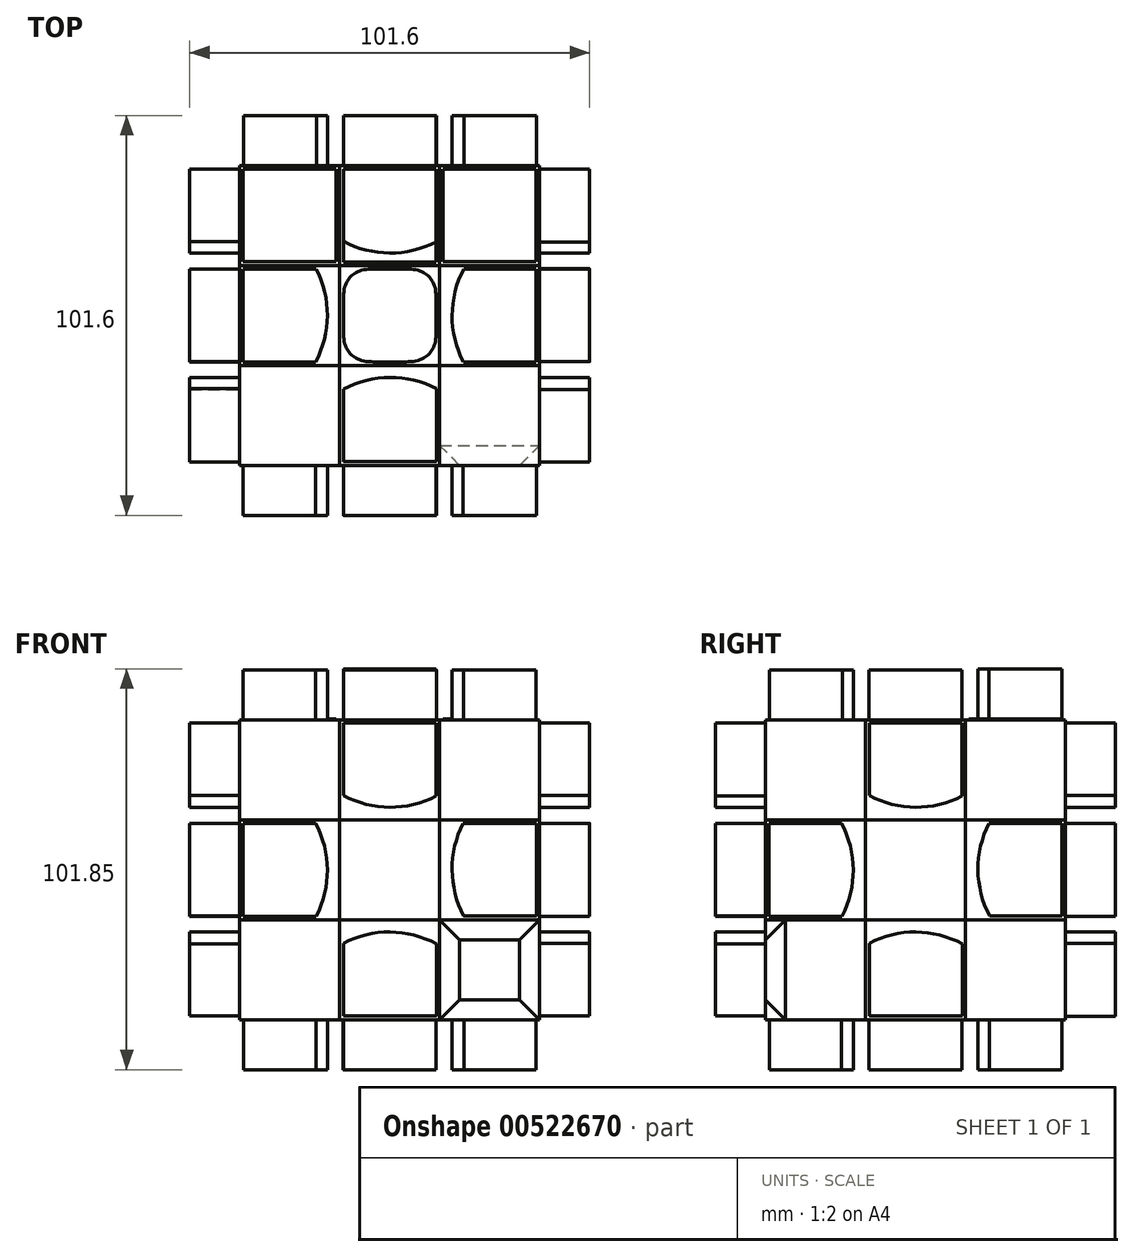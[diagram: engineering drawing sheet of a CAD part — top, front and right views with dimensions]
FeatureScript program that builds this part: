
annotation { "Feature Type Name" : "Feature", "Feature Type Description" : "" }
export const myFeature = defineFeature(function(context is Context, id is Id, definition is map)
    precondition{}
    {
        {
            var Q0;
            Q0=qCreatedBy(makeId("Top.planeOp"),FACE);
            var sketch = newSketch(context, id + "F0", { "sketchPlane" : qUnion([Q0])});
            skLineSegment(sketch, "E0.bottom", {"start": v(12.7, 12.7) * mm, "end": v(-12.7, 12.7) * mm});
            skLineSegment(sketch, "E0.top", {"start": v(12.7, -12.7) * mm, "end": v(-12.7, -12.7) * mm});
            skLineSegment(sketch, "E0.left", {"start": v(12.7, 12.7) * mm, "end": v(12.7, -12.7) * mm});
            skLineSegment(sketch, "E0.right", {"start": v(-12.7, 12.7) * mm, "end": v(-12.7, -12.7) * mm});
            skPoint(sketch, "E0.middle", {"position": v(0, 0) * mm});
            skSolve(sketch);
        }
        {
            var Q0;
            Q0=makeQuery(id+"F0.imprint","IMPRINT",FACE,{"disambiguationData":[TD([[makeQuery(id+"F0.imprint","IMPRINT",EDGE,{"derivedFrom":sQuery(id+"F0.wireOp",EDGE,"E0.bottom")}),1.0]])]});
            var sketch = newSketch(context, id + "F1", { "sketchPlane" : qUnion([Q0])});
            skLineSegment(sketch, "E1.bottom", {"start": v(-12.7, 12.7) * mm, "end": v(-38.1, 12.7) * mm});
            skLineSegment(sketch, "E1.top", {"start": v(-12.7, 38.1) * mm, "end": v(-38.1, 38.1) * mm});
            skLineSegment(sketch, "E1.left", {"start": v(-12.7, 12.7) * mm, "end": v(-12.7, 38.1) * mm});
            skLineSegment(sketch, "E1.right", {"start": v(-38.1, 12.7) * mm, "end": v(-38.1, 38.1) * mm});
            skSolve(sketch);
        }
        {
            var Q0;
            Q0=qCreatedBy(makeId("Top.planeOp"),FACE);
            var sketch = newSketch(context, id + "F2", { "sketchPlane" : qUnion([Q0])});
            skLineSegment(sketch, "E2.bottom", {"start": v(-12.7, 12.7) * mm, "end": v(12.7, 12.7) * mm});
            skLineSegment(sketch, "E2.top", {"start": v(-12.7, 38.1) * mm, "end": v(12.7, 38.1) * mm});
            skLineSegment(sketch, "E2.left", {"start": v(-12.7, 12.7) * mm, "end": v(-12.7, 38.1) * mm});
            skLineSegment(sketch, "E2.right", {"start": v(12.7, 12.7) * mm, "end": v(12.7, 38.1) * mm});
            skSolve(sketch);
        }
        {
            var Q0;
            Q0=qCreatedBy(makeId("Top.planeOp"),FACE);
            var sketch = newSketch(context, id + "F3", { "sketchPlane" : qUnion([Q0])});
            skLineSegment(sketch, "E3.bottom", {"start": v(12.7, 38.1) * mm, "end": v(38.1, 38.1) * mm});
            skLineSegment(sketch, "E3.top", {"start": v(12.7, 12.7) * mm, "end": v(38.1, 12.7) * mm});
            skLineSegment(sketch, "E3.left", {"start": v(12.7, 38.1) * mm, "end": v(12.7, 12.7) * mm});
            skLineSegment(sketch, "E3.right", {"start": v(38.1, 38.1) * mm, "end": v(38.1, 12.7) * mm});
            skSolve(sketch);
        }
        {
            var Q0;
            Q0=qCreatedBy(makeId("Top.planeOp"),FACE);
            var sketch = newSketch(context, id + "F4", { "sketchPlane" : qUnion([Q0])});
            skLineSegment(sketch, "E4.bottom", {"start": v(12.7, 12.7) * mm, "end": v(38.1, 12.7) * mm});
            skLineSegment(sketch, "E4.top", {"start": v(12.7, -12.7) * mm, "end": v(38.1, -12.7) * mm});
            skLineSegment(sketch, "E4.left", {"start": v(12.7, 12.7) * mm, "end": v(12.7, -12.7) * mm});
            skLineSegment(sketch, "E4.right", {"start": v(38.1, 12.7) * mm, "end": v(38.1, -12.7) * mm});
            skSolve(sketch);
        }
        {
            var Q0;
            Q0=qCreatedBy(makeId("Top.planeOp"),FACE);
            var sketch = newSketch(context, id + "F5", { "sketchPlane" : qUnion([Q0])});
            skLineSegment(sketch, "E5.bottom", {"start": v(12.7, -12.7) * mm, "end": v(38.1, -12.7) * mm});
            skLineSegment(sketch, "E5.top", {"start": v(12.7, -38.1) * mm, "end": v(38.1, -38.1) * mm});
            skLineSegment(sketch, "E5.left", {"start": v(12.7, -12.7) * mm, "end": v(12.7, -38.1) * mm});
            skLineSegment(sketch, "E5.right", {"start": v(38.1, -12.7) * mm, "end": v(38.1, -38.1) * mm});
            skSolve(sketch);
        }
        {
            var Q0;
            Q0=qCreatedBy(makeId("Top.planeOp"),FACE);
            var sketch = newSketch(context, id + "F6", { "sketchPlane" : qUnion([Q0])});
            skLineSegment(sketch, "E6.bottom", {"start": v(12.7, -12.7) * mm, "end": v(-12.7, -12.7) * mm});
            skLineSegment(sketch, "E6.top", {"start": v(12.7, -38.1) * mm, "end": v(-12.7, -38.1) * mm});
            skLineSegment(sketch, "E6.left", {"start": v(12.7, -12.7) * mm, "end": v(12.7, -38.1) * mm});
            skLineSegment(sketch, "E6.right", {"start": v(-12.7, -12.7) * mm, "end": v(-12.7, -38.1) * mm});
            skSolve(sketch);
        }
        {
            var Q0;
            Q0=qCreatedBy(makeId("Top.planeOp"),FACE);
            var sketch = newSketch(context, id + "F7", { "sketchPlane" : qUnion([Q0])});
            skLineSegment(sketch, "E7.bottom", {"start": v(-12.7, 12.7) * mm, "end": v(-38.1, 12.7) * mm});
            skLineSegment(sketch, "E7.top", {"start": v(-12.7, -12.7) * mm, "end": v(-38.1, -12.7) * mm});
            skLineSegment(sketch, "E7.left", {"start": v(-12.7, 12.7) * mm, "end": v(-12.7, -12.7) * mm});
            skLineSegment(sketch, "E7.right", {"start": v(-38.1, 12.7) * mm, "end": v(-38.1, -12.7) * mm});
            skSolve(sketch);
        }
        {
            var Q0;
            Q0=qCreatedBy(makeId("Top.planeOp"),FACE);
            var sketch = newSketch(context, id + "F8", { "sketchPlane" : qUnion([Q0])});
            skLineSegment(sketch, "E8.bottom", {"start": v(-12.7, -12.7) * mm, "end": v(-38.1, -12.7) * mm});
            skLineSegment(sketch, "E8.top", {"start": v(-12.7, -38.1) * mm, "end": v(-38.1, -38.1) * mm});
            skLineSegment(sketch, "E8.left", {"start": v(-12.7, -12.7) * mm, "end": v(-12.7, -38.1) * mm});
            skLineSegment(sketch, "E8.right", {"start": v(-38.1, -12.7) * mm, "end": v(-38.1, -38.1) * mm});
            skSolve(sketch);
        }
        {
            var Q0;
            Q0=makeQuery(id+"F1.imprint","IMPRINT",FACE,{"disambiguationData":[TD([[makeQuery(id+"F1.imprint","IMPRINT",EDGE,{"derivedFrom":sQuery(id+"F1.wireOp",EDGE,"E1.bottom")}),-1.0]])]});
            extrude(context, id + "F9", {"entities" : qUnion([Q0]), "depth" : 25.4 * mm, "offsetDistance" : 25.4 * mm});
        }
        {
            var Q0;
            Q0=makeQuery(id+"F2.imprint","IMPRINT",FACE,{"disambiguationData":[TD([[makeQuery(id+"F2.imprint","IMPRINT",EDGE,{"derivedFrom":sQuery(id+"F2.wireOp",EDGE,"E2.bottom")}),1.0]])]});
            extrude(context, id + "F10", {"entities" : qUnion([Q0]), "depth" : 25.4 * mm, "offsetDistance" : 25.4 * mm});
        }
        {
            var Q0;
            Q0=makeQuery(id+"F3.imprint","IMPRINT",FACE,{"disambiguationData":[TD([[makeQuery(id+"F3.imprint","IMPRINT",EDGE,{"derivedFrom":sQuery(id+"F3.wireOp",EDGE,"E3.bottom")}),-1.0]])]});
            extrude(context, id + "F11", {"entities" : qUnion([Q0]), "depth" : 25.4 * mm, "offsetDistance" : 25.4 * mm});
        }
        {
            var Q0;
            Q0=makeQuery(id+"F7.imprint","IMPRINT",FACE,{"disambiguationData":[TD([[makeQuery(id+"F7.imprint","IMPRINT",EDGE,{"derivedFrom":sQuery(id+"F7.wireOp",EDGE,"E7.bottom")}),1.0]])]});
            extrude(context, id + "F12", {"entities" : qUnion([Q0]), "depth" : 25.4 * mm, "offsetDistance" : 25.4 * mm});
        }
        {
            var Q0;
            Q0=makeQuery(id+"F0.imprint","IMPRINT",FACE,{"disambiguationData":[TD([[makeQuery(id+"F0.imprint","IMPRINT",EDGE,{"derivedFrom":sQuery(id+"F0.wireOp",EDGE,"E0.bottom")}),1.0]])]});
            extrude(context, id + "F13", {"entities" : qUnion([Q0]), "depth" : 25.4 * mm, "offsetDistance" : 25.4 * mm});
        }
        {
            var Q0;
            Q0=makeQuery(id+"F4.imprint","IMPRINT",FACE,{"disambiguationData":[TD([[makeQuery(id+"F4.imprint","IMPRINT",EDGE,{"derivedFrom":sQuery(id+"F4.wireOp",EDGE,"E4.bottom")}),-1.0]])]});
            extrude(context, id + "F14", {"entities" : qUnion([Q0]), "depth" : 25.4 * mm, "offsetDistance" : 25.4 * mm});
        }
        {
            var Q0;
            Q0=makeQuery(id+"F8.imprint","IMPRINT",FACE,{"disambiguationData":[TD([[makeQuery(id+"F8.imprint","IMPRINT",EDGE,{"derivedFrom":sQuery(id+"F8.wireOp",EDGE,"E8.bottom")}),1.0]])]});
            extrude(context, id + "F15", {"entities" : qUnion([Q0]), "depth" : 25.4 * mm, "offsetDistance" : 25.4 * mm});
        }
        {
            var Q0;
            Q0=makeQuery(id+"F6.imprint","IMPRINT",FACE,{"disambiguationData":[TD([[makeQuery(id+"F6.imprint","IMPRINT",EDGE,{"derivedFrom":sQuery(id+"F6.wireOp",EDGE,"E6.bottom")}),1.0]])]});
            extrude(context, id + "F16", {"entities" : qUnion([Q0]), "depth" : 25.4 * mm, "offsetDistance" : 25.4 * mm});
        }
        {
            var Q0;
            Q0=makeQuery(id+"F5.imprint","IMPRINT",FACE,{"disambiguationData":[TD([[makeQuery(id+"F5.imprint","IMPRINT",EDGE,{"derivedFrom":sQuery(id+"F5.wireOp",EDGE,"E5.bottom")}),-1.0]])]});
            extrude(context, id + "F17", {"entities" : qUnion([Q0]), "depth" : 25.4 * mm, "offsetDistance" : 25.4 * mm});
        }
        {
            var Q0;
            Q0=makeQuery(id+"F9.opExtrude","CAP_FACE",FACE,{"disambiguationData":[OSD([sQuery(id+"F1.wireOp",EDGE,"E1.bottom"),sQuery(id+"F1.wireOp",EDGE,"E1.top"),sQuery(id+"F1.wireOp",EDGE,"E1.left"),sQuery(id+"F1.wireOp",EDGE,"E1.right")])],"isStart":false});
            var sketch = newSketch(context, id + "F18", { "sketchPlane" : qUnion([Q0])});
            skLineSegment(sketch, "E9.bottom", {"start": v(-12.7, 12.7) * mm, "end": v(-38.1, 12.7) * mm});
            skLineSegment(sketch, "E9.top", {"start": v(-12.7, 38.1) * mm, "end": v(-38.1, 38.1) * mm});
            skLineSegment(sketch, "E9.left", {"start": v(-12.7, 12.7) * mm, "end": v(-12.7, 38.1) * mm});
            skLineSegment(sketch, "E9.right", {"start": v(-38.1, 12.7) * mm, "end": v(-38.1, 38.1) * mm});
            skSolve(sketch);
        }
        {
            var Q0;
            Q0=makeQuery(id+"F10.opExtrude","CAP_FACE",FACE,{"disambiguationData":[OSD([sQuery(id+"F2.wireOp",EDGE,"E2.bottom"),sQuery(id+"F2.wireOp",EDGE,"E2.top"),sQuery(id+"F2.wireOp",EDGE,"E2.left"),sQuery(id+"F2.wireOp",EDGE,"E2.right")])],"isStart":false});
            var sketch = newSketch(context, id + "F19", { "sketchPlane" : qUnion([Q0])});
            skLineSegment(sketch, "E10.bottom", {"start": v(-12.7, 12.7) * mm, "end": v(12.7, 12.7) * mm});
            skLineSegment(sketch, "E10.top", {"start": v(-12.7, 38.1) * mm, "end": v(12.7, 38.1) * mm});
            skLineSegment(sketch, "E10.left", {"start": v(-12.7, 12.7) * mm, "end": v(-12.7, 38.1) * mm});
            skLineSegment(sketch, "E10.right", {"start": v(12.7, 12.7) * mm, "end": v(12.7, 38.1) * mm});
            skSolve(sketch);
        }
        {
            var Q0;
            Q0=makeQuery(id+"F11.opExtrude","CAP_FACE",FACE,{"disambiguationData":[OSD([sQuery(id+"F3.wireOp",EDGE,"E3.bottom"),sQuery(id+"F3.wireOp",EDGE,"E3.top"),sQuery(id+"F3.wireOp",EDGE,"E3.left"),sQuery(id+"F3.wireOp",EDGE,"E3.right")])],"isStart":false});
            var sketch = newSketch(context, id + "F20", { "sketchPlane" : qUnion([Q0])});
            skLineSegment(sketch, "E11.bottom", {"start": v(12.7, 12.7) * mm, "end": v(38.1, 12.7) * mm});
            skLineSegment(sketch, "E11.top", {"start": v(12.7, 38.1) * mm, "end": v(38.1, 38.1) * mm});
            skLineSegment(sketch, "E11.left", {"start": v(12.7, 12.7) * mm, "end": v(12.7, 38.1) * mm});
            skLineSegment(sketch, "E11.right", {"start": v(38.1, 12.7) * mm, "end": v(38.1, 38.1) * mm});
            skSolve(sketch);
        }
        {
            var Q0;
            Q0=makeQuery(id+"F12.opExtrude","CAP_FACE",FACE,{"disambiguationData":[OSD([sQuery(id+"F7.wireOp",EDGE,"E7.bottom"),sQuery(id+"F7.wireOp",EDGE,"E7.top"),sQuery(id+"F7.wireOp",EDGE,"E7.left"),sQuery(id+"F7.wireOp",EDGE,"E7.right")])],"isStart":false});
            var sketch = newSketch(context, id + "F21", { "sketchPlane" : qUnion([Q0])});
            skLineSegment(sketch, "E12.bottom", {"start": v(-38.1, 12.7) * mm, "end": v(-12.7, 12.7) * mm});
            skLineSegment(sketch, "E12.top", {"start": v(-38.1, -12.7) * mm, "end": v(-12.7, -12.7) * mm});
            skLineSegment(sketch, "E12.left", {"start": v(-38.1, 12.7) * mm, "end": v(-38.1, -12.7) * mm});
            skLineSegment(sketch, "E12.right", {"start": v(-12.7, 12.7) * mm, "end": v(-12.7, -12.7) * mm});
            skSolve(sketch);
        }
        {
            var Q0;
            Q0=makeQuery(id+"F14.opExtrude","CAP_FACE",FACE,{"disambiguationData":[OSD([sQuery(id+"F4.wireOp",EDGE,"E4.bottom"),sQuery(id+"F4.wireOp",EDGE,"E4.top"),sQuery(id+"F4.wireOp",EDGE,"E4.left"),sQuery(id+"F4.wireOp",EDGE,"E4.right")])],"isStart":false});
            var sketch = newSketch(context, id + "F22", { "sketchPlane" : qUnion([Q0])});
            skLineSegment(sketch, "E13.bottom", {"start": v(12.7, 12.7) * mm, "end": v(38.1, 12.7) * mm});
            skLineSegment(sketch, "E13.top", {"start": v(12.7, -12.7) * mm, "end": v(38.1, -12.7) * mm});
            skLineSegment(sketch, "E13.left", {"start": v(12.7, 12.7) * mm, "end": v(12.7, -12.7) * mm});
            skLineSegment(sketch, "E13.right", {"start": v(38.1, 12.7) * mm, "end": v(38.1, -12.7) * mm});
            skSolve(sketch);
        }
        {
            var Q0;
            Q0=makeQuery(id+"F15.opExtrude","CAP_FACE",FACE,{"disambiguationData":[OSD([sQuery(id+"F8.wireOp",EDGE,"E8.bottom"),sQuery(id+"F8.wireOp",EDGE,"E8.top"),sQuery(id+"F8.wireOp",EDGE,"E8.left"),sQuery(id+"F8.wireOp",EDGE,"E8.right")])],"isStart":false});
            var sketch = newSketch(context, id + "F23", { "sketchPlane" : qUnion([Q0])});
            skLineSegment(sketch, "E14.bottom", {"start": v(-38.1, -12.7) * mm, "end": v(-12.7, -12.7) * mm});
            skLineSegment(sketch, "E14.top", {"start": v(-38.1, -38.1) * mm, "end": v(-12.7, -38.1) * mm});
            skLineSegment(sketch, "E14.left", {"start": v(-38.1, -12.7) * mm, "end": v(-38.1, -38.1) * mm});
            skLineSegment(sketch, "E14.right", {"start": v(-12.7, -12.7) * mm, "end": v(-12.7, -38.1) * mm});
            skSolve(sketch);
        }
        {
            var Q0;
            Q0=makeQuery(id+"F16.opExtrude","CAP_FACE",FACE,{"disambiguationData":[OSD([sQuery(id+"F6.wireOp",EDGE,"E6.bottom"),sQuery(id+"F6.wireOp",EDGE,"E6.top"),sQuery(id+"F6.wireOp",EDGE,"E6.left"),sQuery(id+"F6.wireOp",EDGE,"E6.right")])],"isStart":false});
            var sketch = newSketch(context, id + "F24", { "sketchPlane" : qUnion([Q0])});
            skLineSegment(sketch, "E15.bottom", {"start": v(-12.7, -12.7) * mm, "end": v(12.7, -12.7) * mm});
            skLineSegment(sketch, "E15.top", {"start": v(-12.7, -38.1) * mm, "end": v(12.7, -38.1) * mm});
            skLineSegment(sketch, "E15.left", {"start": v(-12.7, -12.7) * mm, "end": v(-12.7, -38.1) * mm});
            skLineSegment(sketch, "E15.right", {"start": v(12.7, -12.7) * mm, "end": v(12.7, -38.1) * mm});
            skSolve(sketch);
        }
        {
            var Q0;
            Q0=makeQuery(id+"F17.opExtrude","CAP_FACE",FACE,{"disambiguationData":[OSD([sQuery(id+"F5.wireOp",EDGE,"E5.bottom"),sQuery(id+"F5.wireOp",EDGE,"E5.top"),sQuery(id+"F5.wireOp",EDGE,"E5.left"),sQuery(id+"F5.wireOp",EDGE,"E5.right")])],"isStart":false});
            var sketch = newSketch(context, id + "F25", { "sketchPlane" : qUnion([Q0])});
            skLineSegment(sketch, "E16.bottom", {"start": v(12.7, -12.7) * mm, "end": v(38.1, -12.7) * mm});
            skLineSegment(sketch, "E16.top", {"start": v(12.7, -38.1) * mm, "end": v(38.1, -38.1) * mm});
            skLineSegment(sketch, "E16.left", {"start": v(12.7, -12.7) * mm, "end": v(12.7, -38.1) * mm});
            skLineSegment(sketch, "E16.right", {"start": v(38.1, -12.7) * mm, "end": v(38.1, -38.1) * mm});
            skSolve(sketch);
        }
        {
            var Q0;
            Q0=makeQuery(id+"F18.imprint","IMPRINT",FACE,{"disambiguationData":[TD([[makeQuery(id+"F18.imprint","IMPRINT",EDGE,{"derivedFrom":sQuery(id+"F18.wireOp",EDGE,"E9.bottom")}),-1.0]])]});
            extrude(context, id + "F26", {"entities" : qUnion([Q0]), "depth" : 25.4 * mm, "offsetDistance" : 25.4 * mm});
        }
        {
            var Q0;
            Q0=makeQuery(id+"F19.imprint","IMPRINT",FACE,{"disambiguationData":[TD([[makeQuery(id+"F19.imprint","IMPRINT",EDGE,{"derivedFrom":sQuery(id+"F19.wireOp",EDGE,"E10.bottom")}),1.0]])]});
            extrude(context, id + "F27", {"entities" : qUnion([Q0]), "depth" : 25.4 * mm, "offsetDistance" : 25.4 * mm});
        }
        {
            var Q0;
            Q0=makeQuery(id+"F20.imprint","IMPRINT",FACE,{"disambiguationData":[TD([[makeQuery(id+"F20.imprint","IMPRINT",EDGE,{"derivedFrom":sQuery(id+"F20.wireOp",EDGE,"E11.bottom")}),1.0]])]});
            extrude(context, id + "F28", {"entities" : qUnion([Q0]), "depth" : 25.4 * mm, "offsetDistance" : 25.4 * mm});
        }
        {
            var Q0;
            Q0=makeQuery(id+"F21.imprint","IMPRINT",FACE,{"disambiguationData":[TD([[makeQuery(id+"F21.imprint","IMPRINT",EDGE,{"derivedFrom":sQuery(id+"F21.wireOp",EDGE,"E12.bottom")}),1.0]])]});
            extrude(context, id + "F29", {"entities" : qUnion([Q0]), "depth" : 25.4 * mm, "offsetDistance" : 25.4 * mm});
        }
        {
            var Q0;
            Q0=makeQuery(id+"F22.imprint","IMPRINT",FACE,{"disambiguationData":[TD([[makeQuery(id+"F22.imprint","IMPRINT",EDGE,{"derivedFrom":sQuery(id+"F22.wireOp",EDGE,"E13.bottom")}),-1.0]])]});
            extrude(context, id + "F30", {"entities" : qUnion([Q0]), "depth" : 25.4 * mm, "offsetDistance" : 25.4 * mm});
        }
        {
            var Q0;
            Q0=makeQuery(id+"F23.imprint","IMPRINT",FACE,{"disambiguationData":[TD([[makeQuery(id+"F23.imprint","IMPRINT",EDGE,{"derivedFrom":sQuery(id+"F23.wireOp",EDGE,"E14.bottom")}),1.0]])]});
            extrude(context, id + "F31", {"entities" : qUnion([Q0]), "depth" : 25.4 * mm, "offsetDistance" : 25.4 * mm});
        }
        {
            var Q0;
            Q0=makeQuery(id+"F24.imprint","IMPRINT",FACE,{"disambiguationData":[TD([[makeQuery(id+"F24.imprint","IMPRINT",EDGE,{"derivedFrom":sQuery(id+"F24.wireOp",EDGE,"E15.bottom")}),1.0]])]});
            extrude(context, id + "F32", {"entities" : qUnion([Q0]), "depth" : 25.4 * mm, "offsetDistance" : 25.4 * mm});
        }
        {
            var Q0;
            Q0=makeQuery(id+"F25.imprint","IMPRINT",FACE,{"disambiguationData":[TD([[makeQuery(id+"F25.imprint","IMPRINT",EDGE,{"derivedFrom":sQuery(id+"F25.wireOp",EDGE,"E16.bottom")}),-1.0]])]});
            extrude(context, id + "F33", {"entities" : qUnion([Q0]), "depth" : 25.4 * mm, "offsetDistance" : 25.4 * mm});
        }
        {
            var Q0;
            Q0=makeQuery(id+"F13.opExtrude","CAP_FACE",FACE,{"disambiguationData":[OSD([sQuery(id+"F0.wireOp",EDGE,"E0.bottom"),sQuery(id+"F0.wireOp",EDGE,"E0.top"),sQuery(id+"F0.wireOp",EDGE,"E0.left"),sQuery(id+"F0.wireOp",EDGE,"E0.right")])],"isStart":false});
            var sketch = newSketch(context, id + "F34", { "sketchPlane" : qUnion([Q0])});
            skSolve(sketch);
        }
        {
            var Q0;
            Q0=makeQuery(id+"F34.imprint","IMPRINT",FACE,{"disambiguationData":[TD([[makeQuery(id+"F34.imprint","IMPRINT",EDGE,{"derivedFrom":makeQuery(id+"F13.opExtrude","CAP_EDGE",EDGE,{"disambiguationData":[OSD([sQuery(id+"F0.wireOp",EDGE,"E0.bottom")])],"isStart":false})}),1.0]])]});
            extrude(context, id + "F35", {"entities" : qUnion([Q0]), "depth" : 25.4 * mm, "offsetDistance" : 25.4 * mm});
        }
        {
            var Q0;
            Q0=makeQuery(id+"F26.opExtrude","CAP_FACE",FACE,{"disambiguationData":[OSD([sQuery(id+"F18.wireOp",EDGE,"E9.bottom"),sQuery(id+"F18.wireOp",EDGE,"E9.top"),sQuery(id+"F18.wireOp",EDGE,"E9.left"),sQuery(id+"F18.wireOp",EDGE,"E9.right")])],"isStart":false});
            var sketch = newSketch(context, id + "F36", { "sketchPlane" : qUnion([Q0])});
            skSolve(sketch);
        }
        {
            var Q0;
            Q0=makeQuery(id+"F27.opExtrude","CAP_FACE",FACE,{"disambiguationData":[OSD([sQuery(id+"F19.wireOp",EDGE,"E10.bottom"),sQuery(id+"F19.wireOp",EDGE,"E10.top"),sQuery(id+"F19.wireOp",EDGE,"E10.left"),sQuery(id+"F19.wireOp",EDGE,"E10.right")])],"isStart":false});
            var sketch = newSketch(context, id + "F37", { "sketchPlane" : qUnion([Q0])});
            skSolve(sketch);
        }
        {
            var Q0;
            Q0=makeQuery(id+"F29.opExtrude","CAP_FACE",FACE,{"disambiguationData":[OSD([sQuery(id+"F21.wireOp",EDGE,"E12.bottom"),sQuery(id+"F21.wireOp",EDGE,"E12.top"),sQuery(id+"F21.wireOp",EDGE,"E12.left"),sQuery(id+"F21.wireOp",EDGE,"E12.right")])],"isStart":false});
            var sketch = newSketch(context, id + "F38", { "sketchPlane" : qUnion([Q0])});
            skSolve(sketch);
        }
        {
            var Q0;
            Q0=makeQuery(id+"F31.opExtrude","CAP_FACE",FACE,{"disambiguationData":[OSD([sQuery(id+"F23.wireOp",EDGE,"E14.bottom"),sQuery(id+"F23.wireOp",EDGE,"E14.top"),sQuery(id+"F23.wireOp",EDGE,"E14.left"),sQuery(id+"F23.wireOp",EDGE,"E14.right")])],"isStart":false});
            var sketch = newSketch(context, id + "F39", { "sketchPlane" : qUnion([Q0])});
            skSolve(sketch);
        }
        {
            var Q0;
            Q0=makeQuery(id+"F32.opExtrude","CAP_FACE",FACE,{"disambiguationData":[OSD([sQuery(id+"F24.wireOp",EDGE,"E15.bottom"),sQuery(id+"F24.wireOp",EDGE,"E15.top"),sQuery(id+"F24.wireOp",EDGE,"E15.left"),sQuery(id+"F24.wireOp",EDGE,"E15.right")])],"isStart":false});
            var sketch = newSketch(context, id + "F40", { "sketchPlane" : qUnion([Q0])});
            skSolve(sketch);
        }
        {
            var Q0;
            Q0=makeQuery(id+"F33.opExtrude","CAP_FACE",FACE,{"disambiguationData":[OSD([sQuery(id+"F25.wireOp",EDGE,"E16.bottom"),sQuery(id+"F25.wireOp",EDGE,"E16.top"),sQuery(id+"F25.wireOp",EDGE,"E16.left"),sQuery(id+"F25.wireOp",EDGE,"E16.right")])],"isStart":false});
            var sketch = newSketch(context, id + "F41", { "sketchPlane" : qUnion([Q0])});
            skSolve(sketch);
        }
        {
            var Q0;
            Q0=makeQuery(id+"F30.opExtrude","CAP_FACE",FACE,{"disambiguationData":[OSD([sQuery(id+"F22.wireOp",EDGE,"E13.bottom"),sQuery(id+"F22.wireOp",EDGE,"E13.top"),sQuery(id+"F22.wireOp",EDGE,"E13.left"),sQuery(id+"F22.wireOp",EDGE,"E13.right")])],"isStart":false});
            var sketch = newSketch(context, id + "F42", { "sketchPlane" : qUnion([Q0])});
            skSolve(sketch);
        }
        {
            var Q0;
            Q0=makeQuery(id+"F28.opExtrude","CAP_FACE",FACE,{"disambiguationData":[OSD([sQuery(id+"F20.wireOp",EDGE,"E11.bottom"),sQuery(id+"F20.wireOp",EDGE,"E11.top"),sQuery(id+"F20.wireOp",EDGE,"E11.left"),sQuery(id+"F20.wireOp",EDGE,"E11.right")])],"isStart":false});
            var sketch = newSketch(context, id + "F43", { "sketchPlane" : qUnion([Q0])});
            skSolve(sketch);
        }
        {
            var Q0;
            Q0=makeQuery(id+"F35.opExtrude","CAP_FACE",FACE,{"disambiguationData":[OSD([sQuery(id+"F0.wireOp",EDGE,"E0.bottom"),sQuery(id+"F0.wireOp",EDGE,"E0.top"),sQuery(id+"F0.wireOp",EDGE,"E0.left"),sQuery(id+"F0.wireOp",EDGE,"E0.right")])],"isStart":false});
            var sketch = newSketch(context, id + "F44", { "sketchPlane" : qUnion([Q0])});
            skSolve(sketch);
        }
        {
            var Q0;
            Q0=makeQuery(id+"F36.imprint","IMPRINT",FACE,{"disambiguationData":[TD([[makeQuery(id+"F36.imprint","IMPRINT",EDGE,{"derivedFrom":makeQuery(id+"F26.opExtrude","CAP_EDGE",EDGE,{"disambiguationData":[OSD([sQuery(id+"F18.wireOp",EDGE,"E9.bottom")])],"isStart":false})}),-1.0]])]});
            extrude(context, id + "F45", {"entities" : qUnion([Q0]), "depth" : 25.4 * mm, "offsetDistance" : 25.4 * mm});
        }
        {
            var Q0;
            Q0=makeQuery(id+"F38.imprint","IMPRINT",FACE,{"disambiguationData":[TD([[makeQuery(id+"F38.imprint","IMPRINT",EDGE,{"derivedFrom":makeQuery(id+"F29.opExtrude","CAP_EDGE",EDGE,{"disambiguationData":[OSD([sQuery(id+"F21.wireOp",EDGE,"E12.bottom")])],"isStart":false})}),1.0]])]});
            extrude(context, id + "F46", {"entities" : qUnion([Q0]), "depth" : 25.4 * mm, "offsetDistance" : 25.4 * mm});
        }
        {
            var Q0;
            Q0=makeQuery(id+"F39.imprint","IMPRINT",FACE,{"disambiguationData":[TD([[makeQuery(id+"F39.imprint","IMPRINT",EDGE,{"derivedFrom":makeQuery(id+"F31.opExtrude","CAP_EDGE",EDGE,{"disambiguationData":[OSD([sQuery(id+"F23.wireOp",EDGE,"E14.bottom")])],"isStart":false})}),1.0]])]});
            extrude(context, id + "F47", {"entities" : qUnion([Q0]), "depth" : 25.4 * mm, "offsetDistance" : 25.4 * mm});
        }
        {
            var Q0;
            Q0=makeQuery(id+"F37.imprint","IMPRINT",FACE,{"disambiguationData":[TD([[makeQuery(id+"F37.imprint","IMPRINT",EDGE,{"derivedFrom":makeQuery(id+"F27.opExtrude","CAP_EDGE",EDGE,{"disambiguationData":[OSD([sQuery(id+"F19.wireOp",EDGE,"E10.bottom")])],"isStart":false})}),1.0]])]});
            extrude(context, id + "F48", {"entities" : qUnion([Q0]), "depth" : 25.4 * mm, "offsetDistance" : 25.4 * mm});
        }
        {
            var Q0;
            Q0=makeQuery(id+"F44.imprint","IMPRINT",FACE,{"disambiguationData":[TD([[makeQuery(id+"F44.imprint","IMPRINT",EDGE,{"derivedFrom":makeQuery(id+"F35.opExtrude","CAP_EDGE",EDGE,{"disambiguationData":[OSD([sQuery(id+"F0.wireOp",EDGE,"E0.bottom")])],"isStart":false})}),1.0]])]});
            extrude(context, id + "F49", {"entities" : qUnion([Q0]), "depth" : 25.4 * mm, "offsetDistance" : 25.4 * mm});
        }
        {
            var Q0;
            Q0=makeQuery(id+"F40.imprint","IMPRINT",FACE,{"disambiguationData":[TD([[makeQuery(id+"F40.imprint","IMPRINT",EDGE,{"derivedFrom":makeQuery(id+"F32.opExtrude","CAP_EDGE",EDGE,{"disambiguationData":[OSD([sQuery(id+"F24.wireOp",EDGE,"E15.bottom")])],"isStart":false})}),1.0]])]});
            extrude(context, id + "F50", {"entities" : qUnion([Q0]), "depth" : 25.4 * mm, "offsetDistance" : 25.4 * mm});
        }
        {
            var Q0;
            Q0=makeQuery(id+"F41.imprint","IMPRINT",FACE,{"disambiguationData":[TD([[makeQuery(id+"F41.imprint","IMPRINT",EDGE,{"derivedFrom":makeQuery(id+"F33.opExtrude","CAP_EDGE",EDGE,{"disambiguationData":[OSD([sQuery(id+"F25.wireOp",EDGE,"E16.bottom")])],"isStart":false})}),-1.0]])]});
            extrude(context, id + "F51", {"entities" : qUnion([Q0]), "depth" : 25.4 * mm, "offsetDistance" : 25.4 * mm});
        }
        {
            var Q0;
            Q0=makeQuery(id+"F42.imprint","IMPRINT",FACE,{"disambiguationData":[TD([[makeQuery(id+"F42.imprint","IMPRINT",EDGE,{"derivedFrom":makeQuery(id+"F30.opExtrude","CAP_EDGE",EDGE,{"disambiguationData":[OSD([sQuery(id+"F22.wireOp",EDGE,"E13.bottom")])],"isStart":false})}),-1.0]])]});
            extrude(context, id + "F52", {"entities" : qUnion([Q0]), "depth" : 25.4 * mm, "offsetDistance" : 25.4 * mm});
        }
        {
            var Q0;
            Q0=makeQuery(id+"F43.imprint","IMPRINT",FACE,{"disambiguationData":[TD([[makeQuery(id+"F43.imprint","IMPRINT",EDGE,{"derivedFrom":makeQuery(id+"F28.opExtrude","CAP_EDGE",EDGE,{"disambiguationData":[OSD([sQuery(id+"F20.wireOp",EDGE,"E11.bottom")])],"isStart":false})}),1.0]])]});
            extrude(context, id + "F53", {"entities" : qUnion([Q0]), "depth" : 25.4 * mm, "offsetDistance" : 25.4 * mm});
        }
        {
            var Q0;
            Q0=makeQuery(id+"F46.opExtrude","CAP_FACE",FACE,{"disambiguationData":[OSD([sQuery(id+"F21.wireOp",EDGE,"E12.bottom"),sQuery(id+"F21.wireOp",EDGE,"E12.top"),sQuery(id+"F21.wireOp",EDGE,"E12.left"),sQuery(id+"F21.wireOp",EDGE,"E12.right")])],"isStart":false});
            var sketch = newSketch(context, id + "F54", { "sketchPlane" : qUnion([Q0])});
            skLineSegment(sketch, "E17.bottom", {"start": v(-37.22, 11.78) * mm, "end": v(-13.61, 11.78) * mm});
            skLineSegment(sketch, "E17.top", {"start": v(-37.22, -11.82) * mm, "end": v(-13.61, -11.82) * mm});
            skLineSegment(sketch, "E17.left", {"start": v(-37.22, 11.78) * mm, "end": v(-37.22, -11.82) * mm});
            skLineSegment(sketch, "E17.right", {"start": v(-13.61, 11.78) * mm, "end": v(-13.61, -11.82) * mm});
            skSolve(sketch);
        }
        {
            var Q0;
            Q0=makeQuery(id+"F45.opExtrude","CAP_FACE",FACE,{"disambiguationData":[OSD([sQuery(id+"F18.wireOp",EDGE,"E9.bottom"),sQuery(id+"F18.wireOp",EDGE,"E9.top"),sQuery(id+"F18.wireOp",EDGE,"E9.left"),sQuery(id+"F18.wireOp",EDGE,"E9.right")])],"isStart":false});
            var sketch = newSketch(context, id + "F55", { "sketchPlane" : qUnion([Q0])});
            skLineSegment(sketch, "E18.bottom", {"start": v(-37.21, 37.2) * mm, "end": v(-13.6, 37.2) * mm});
            skLineSegment(sketch, "E18.top", {"start": v(-37.21, 13.6) * mm, "end": v(-13.6, 13.6) * mm});
            skLineSegment(sketch, "E18.left", {"start": v(-37.21, 37.2) * mm, "end": v(-37.21, 13.6) * mm});
            skLineSegment(sketch, "E18.right", {"start": v(-13.6, 37.2) * mm, "end": v(-13.6, 13.6) * mm});
            skSolve(sketch);
        }
        {
            var Q0;
            Q0=makeQuery(id+"F48.opExtrude","CAP_FACE",FACE,{"disambiguationData":[OSD([sQuery(id+"F19.wireOp",EDGE,"E10.bottom"),sQuery(id+"F19.wireOp",EDGE,"E10.top"),sQuery(id+"F19.wireOp",EDGE,"E10.left"),sQuery(id+"F19.wireOp",EDGE,"E10.right")])],"isStart":false});
            var sketch = newSketch(context, id + "F56", { "sketchPlane" : qUnion([Q0])});
            skLineSegment(sketch, "E19.bottom", {"start": v(-11.8, 37.2) * mm, "end": v(11.79, 37.2) * mm});
            skLineSegment(sketch, "E19.top", {"start": v(-11.8, 13.58) * mm, "end": v(11.79, 13.58) * mm});
            skLineSegment(sketch, "E19.left", {"start": v(-11.8, 37.2) * mm, "end": v(-11.8, 13.58) * mm});
            skLineSegment(sketch, "E19.right", {"start": v(11.79, 37.2) * mm, "end": v(11.79, 13.58) * mm});
            skSolve(sketch);
        }
        {
            var Q0;
            Q0=makeQuery(id+"F49.opExtrude","CAP_FACE",FACE,{"disambiguationData":[OSD([sQuery(id+"F0.wireOp",EDGE,"E0.bottom"),sQuery(id+"F0.wireOp",EDGE,"E0.top"),sQuery(id+"F0.wireOp",EDGE,"E0.left"),sQuery(id+"F0.wireOp",EDGE,"E0.right")])],"isStart":false});
            var sketch = newSketch(context, id + "F57", { "sketchPlane" : qUnion([Q0])});
            skLineSegment(sketch, "E20.bottom", {"start": v(-11.8, 11.81) * mm, "end": v(11.8, 11.81) * mm});
            skLineSegment(sketch, "E20.top", {"start": v(-11.8, -11.81) * mm, "end": v(11.8, -11.81) * mm});
            skLineSegment(sketch, "E20.left", {"start": v(-11.8, 11.81) * mm, "end": v(-11.8, -11.81) * mm});
            skLineSegment(sketch, "E20.right", {"start": v(11.8, 11.81) * mm, "end": v(11.8, -11.81) * mm});
            skSolve(sketch);
        }
        {
            var Q0;
            Q0=makeQuery(id+"F50.opExtrude","CAP_FACE",FACE,{"disambiguationData":[OSD([sQuery(id+"F24.wireOp",EDGE,"E15.bottom"),sQuery(id+"F24.wireOp",EDGE,"E15.top"),sQuery(id+"F24.wireOp",EDGE,"E15.left"),sQuery(id+"F24.wireOp",EDGE,"E15.right")])],"isStart":false});
            var sketch = newSketch(context, id + "F58", { "sketchPlane" : qUnion([Q0])});
            skLineSegment(sketch, "E21.bottom", {"start": v(-11.72, -13.51) * mm, "end": v(11.88, -13.51) * mm});
            skLineSegment(sketch, "E21.top", {"start": v(-11.72, -37.13) * mm, "end": v(11.88, -37.13) * mm});
            skLineSegment(sketch, "E21.left", {"start": v(-11.72, -13.51) * mm, "end": v(-11.72, -37.13) * mm});
            skLineSegment(sketch, "E21.right", {"start": v(11.88, -13.51) * mm, "end": v(11.88, -37.13) * mm});
            skSolve(sketch);
        }
        {
            var Q0;
            Q0=makeQuery(id+"F53.opExtrude","CAP_FACE",FACE,{"disambiguationData":[OSD([sQuery(id+"F20.wireOp",EDGE,"E11.bottom"),sQuery(id+"F20.wireOp",EDGE,"E11.top"),sQuery(id+"F20.wireOp",EDGE,"E11.left"),sQuery(id+"F20.wireOp",EDGE,"E11.right")])],"isStart":false});
            var sketch = newSketch(context, id + "F59", { "sketchPlane" : qUnion([Q0])});
            skLineSegment(sketch, "E22.bottom", {"start": v(13.59, 37.2) * mm, "end": v(37.2, 37.2) * mm});
            skLineSegment(sketch, "E22.top", {"start": v(13.59, 13.6) * mm, "end": v(37.2, 13.6) * mm});
            skLineSegment(sketch, "E22.left", {"start": v(13.59, 37.2) * mm, "end": v(13.59, 13.6) * mm});
            skLineSegment(sketch, "E22.right", {"start": v(37.2, 37.2) * mm, "end": v(37.2, 13.6) * mm});
            skSolve(sketch);
        }
        {
            var Q0;
            Q0=makeQuery(id+"F52.opExtrude","CAP_FACE",FACE,{"disambiguationData":[OSD([sQuery(id+"F22.wireOp",EDGE,"E13.bottom"),sQuery(id+"F22.wireOp",EDGE,"E13.top"),sQuery(id+"F22.wireOp",EDGE,"E13.left"),sQuery(id+"F22.wireOp",EDGE,"E13.right")])],"isStart":false});
            var sketch = newSketch(context, id + "F60", { "sketchPlane" : qUnion([Q0])});
            skLineSegment(sketch, "E23.bottom", {"start": v(13.6, 11.8) * mm, "end": v(37.18, 11.8) * mm});
            skLineSegment(sketch, "E23.top", {"start": v(13.6, -11.83) * mm, "end": v(37.18, -11.83) * mm});
            skLineSegment(sketch, "E23.left", {"start": v(13.6, 11.8) * mm, "end": v(13.6, -11.83) * mm});
            skLineSegment(sketch, "E23.right", {"start": v(37.18, 11.8) * mm, "end": v(37.18, -11.83) * mm});
            skSolve(sketch);
        }
        {
            var Q0;
            Q0=makeQuery(id+"F55.imprint","IMPRINT",FACE,{"disambiguationData":[TD([[makeQuery(id+"F55.imprint","IMPRINT",EDGE,{"derivedFrom":sQuery(id+"F55.wireOp",EDGE,"E18.bottom")}),-1.0]])]});
            extrude(context, id + "F61", {"entities" : qUnion([Q0]), "depth" : 0.25 * mm, "offsetDistance" : 25.4 * mm});
        }
        {
            var Q0;
            Q0=makeQuery(id+"F56.imprint","IMPRINT",FACE,{"disambiguationData":[TD([[makeQuery(id+"F56.imprint","IMPRINT",EDGE,{"derivedFrom":sQuery(id+"F56.wireOp",EDGE,"E19.bottom")}),-1.0]])]});
            extrude(context, id + "F62", {"entities" : qUnion([Q0]), "depth" : 0.25 * mm, "offsetDistance" : 25.4 * mm});
        }
        {
            var Q0;
            Q0=makeQuery(id+"F59.imprint","IMPRINT",FACE,{"disambiguationData":[TD([[makeQuery(id+"F59.imprint","IMPRINT",EDGE,{"derivedFrom":sQuery(id+"F59.wireOp",EDGE,"E22.bottom")}),-1.0]])]});
            extrude(context, id + "F63", {"entities" : qUnion([Q0]), "depth" : 0.25 * mm, "offsetDistance" : 25.4 * mm});
        }
        {
            var Q0;
            Q0=makeQuery(id+"F54.imprint","IMPRINT",FACE,{"disambiguationData":[TD([[makeQuery(id+"F54.imprint","IMPRINT",EDGE,{"derivedFrom":sQuery(id+"F54.wireOp",EDGE,"E17.bottom")}),-1.0]])]});
            var Q1;
            Q1=makeQuery(id+"F57.imprint","IMPRINT",FACE,{"disambiguationData":[TD([[makeQuery(id+"F57.imprint","IMPRINT",EDGE,{"derivedFrom":sQuery(id+"F57.wireOp",EDGE,"E20.bottom")}),-1.0]])]});
            var Q2;
            Q2=makeQuery(id+"F60.imprint","IMPRINT",FACE,{"disambiguationData":[TD([[makeQuery(id+"F60.imprint","IMPRINT",EDGE,{"derivedFrom":sQuery(id+"F60.wireOp",EDGE,"E23.bottom")}),-1.0]])]});
            var Q3;
            Q3=makeQuery(id+"F58.imprint","IMPRINT",FACE,{"disambiguationData":[TD([[makeQuery(id+"F58.imprint","IMPRINT",EDGE,{"derivedFrom":sQuery(id+"F58.wireOp",EDGE,"E21.bottom")}),-1.0]])]});
            var Q4;
            Q4=makeQuery(id+"F62.opExtrude","CAP_FACE",FACE,{"disambiguationData":[OSD([sQuery(id+"F56.wireOp",EDGE,"E19.bottom"),sQuery(id+"F56.wireOp",EDGE,"E19.top"),sQuery(id+"F56.wireOp",EDGE,"E19.left"),sQuery(id+"F56.wireOp",EDGE,"E19.right")])],"isStart":false});
            extrude(context, id + "F64", {"entities" : qUnion([Q0, Q1, Q2, Q3, Q4]), "depth" : 12.7 * mm, "offsetDistance" : 25.4 * mm});
        }
        {
            var Q0;
            Q0=makeQuery(id+"F26.opExtrude","SWEPT_FACE",FACE,{"disambiguationData":[OSD([sQuery(id+"F18.wireOp",EDGE,"E9.right")])]});
            var sketch = newSketch(context, id + "F65", { "sketchPlane" : qUnion([Q0])});
            skLineSegment(sketch, "E24.bottom", {"start": v(-37.21, 49.89) * mm, "end": v(-13.6, 49.89) * mm});
            skLineSegment(sketch, "E24.top", {"start": v(-37.21, 26.29) * mm, "end": v(-13.6, 26.29) * mm});
            skLineSegment(sketch, "E24.left", {"start": v(-37.21, 49.89) * mm, "end": v(-37.21, 26.29) * mm});
            skLineSegment(sketch, "E24.right", {"start": v(-13.6, 49.89) * mm, "end": v(-13.6, 26.29) * mm});
            skSolve(sketch);
        }
        {
            var Q0;
            Q0=makeQuery(id+"F46.opExtrude","SWEPT_FACE",FACE,{"disambiguationData":[OSD([sQuery(id+"F21.wireOp",EDGE,"E12.left")])]});
            var sketch = newSketch(context, id + "F66", { "sketchPlane" : qUnion([Q0])});
            skLineSegment(sketch, "E25.bottom", {"start": v(-11.76, 75.35) * mm, "end": v(11.8, 75.35) * mm});
            skLineSegment(sketch, "E25.top", {"start": v(-11.76, 51.69) * mm, "end": v(11.8, 51.69) * mm});
            skLineSegment(sketch, "E25.left", {"start": v(-11.76, 75.35) * mm, "end": v(-11.76, 51.69) * mm});
            skLineSegment(sketch, "E25.right", {"start": v(11.8, 75.35) * mm, "end": v(11.8, 51.69) * mm});
            skSolve(sketch);
        }
        {
            var Q0;
            Q0=makeQuery(id+"F29.opExtrude","SWEPT_FACE",FACE,{"disambiguationData":[OSD([sQuery(id+"F21.wireOp",EDGE,"E12.left")])]});
            var sketch = newSketch(context, id + "F67", { "sketchPlane" : qUnion([Q0])});
            skLineSegment(sketch, "E26.bottom", {"start": v(-11.8, 49.9) * mm, "end": v(11.8, 49.9) * mm});
            skLineSegment(sketch, "E26.top", {"start": v(-11.8, 26.3) * mm, "end": v(11.8, 26.3) * mm});
            skLineSegment(sketch, "E26.left", {"start": v(-11.8, 49.9) * mm, "end": v(-11.8, 26.3) * mm});
            skLineSegment(sketch, "E26.right", {"start": v(11.8, 49.9) * mm, "end": v(11.8, 26.3) * mm});
            skSolve(sketch);
        }
        {
            var Q0;
            Q0=makeQuery(id+"F12.opExtrude","SWEPT_FACE",FACE,{"disambiguationData":[OSD([sQuery(id+"F7.wireOp",EDGE,"E7.right")])]});
            var sketch = newSketch(context, id + "F68", { "sketchPlane" : qUnion([Q0])});
            skLineSegment(sketch, "E27.bottom", {"start": v(-11.8, 24.5) * mm, "end": v(11.83, 24.5) * mm});
            skLineSegment(sketch, "E27.top", {"start": v(-11.8, 0.92) * mm, "end": v(11.83, 0.92) * mm});
            skLineSegment(sketch, "E27.left", {"start": v(-11.8, 24.5) * mm, "end": v(-11.8, 0.92) * mm});
            skLineSegment(sketch, "E27.right", {"start": v(11.83, 24.5) * mm, "end": v(11.83, 0.92) * mm});
            skSolve(sketch);
        }
        {
            var Q0;
            Q0=makeQuery(id+"F31.opExtrude","SWEPT_FACE",FACE,{"disambiguationData":[OSD([sQuery(id+"F23.wireOp",EDGE,"E14.left")])]});
            var sketch = newSketch(context, id + "F69", { "sketchPlane" : qUnion([Q0])});
            skLineSegment(sketch, "E28.bottom", {"start": v(13.56, 49.87) * mm, "end": v(37.21, 49.87) * mm});
            skLineSegment(sketch, "E28.top", {"start": v(13.56, 26.3) * mm, "end": v(37.21, 26.3) * mm});
            skLineSegment(sketch, "E28.left", {"start": v(13.56, 49.87) * mm, "end": v(13.56, 26.3) * mm});
            skLineSegment(sketch, "E28.right", {"start": v(37.21, 49.87) * mm, "end": v(37.21, 26.3) * mm});
            skSolve(sketch);
        }
        {
            var Q0;
            Q0=makeQuery(id+"F66.imprint","IMPRINT",FACE,{"disambiguationData":[TD([[makeQuery(id+"F66.imprint","IMPRINT",EDGE,{"derivedFrom":sQuery(id+"F66.wireOp",EDGE,"E25.bottom")}),-1.0]])]});
            var Q1;
            Q1=makeQuery(id+"F69.imprint","IMPRINT",FACE,{"disambiguationData":[TD([[makeQuery(id+"F69.imprint","IMPRINT",EDGE,{"derivedFrom":sQuery(id+"F69.wireOp",EDGE,"E28.bottom")}),-1.0]])]});
            var Q2;
            Q2=makeQuery(id+"F65.imprint","IMPRINT",FACE,{"disambiguationData":[TD([[makeQuery(id+"F65.imprint","IMPRINT",EDGE,{"derivedFrom":sQuery(id+"F65.wireOp",EDGE,"E24.bottom")}),-1.0]])]});
            var Q3;
            Q3=makeQuery(id+"F68.imprint","IMPRINT",FACE,{"disambiguationData":[TD([[makeQuery(id+"F68.imprint","IMPRINT",EDGE,{"derivedFrom":sQuery(id+"F68.wireOp",EDGE,"E27.bottom")}),-1.0]])]});
            extrude(context, id + "F70", {"entities" : qUnion([Q0, Q1, Q2, Q3]), "depth" : 12.7 * mm, "offsetDistance" : 25.4 * mm});
        }
        {
            var Q0;
            Q0=makeQuery(id+"F48.opExtrude","SWEPT_FACE",FACE,{"disambiguationData":[OSD([sQuery(id+"F19.wireOp",EDGE,"E10.top")])]});
            var sketch = newSketch(context, id + "F71", { "sketchPlane" : qUnion([Q0])});
            skLineSegment(sketch, "E29.bottom", {"start": v(-11.78, 75.33) * mm, "end": v(11.8, 75.33) * mm});
            skLineSegment(sketch, "E29.top", {"start": v(-11.78, 51.7) * mm, "end": v(11.8, 51.7) * mm});
            skLineSegment(sketch, "E29.left", {"start": v(-11.78, 75.33) * mm, "end": v(-11.78, 51.7) * mm});
            skLineSegment(sketch, "E29.right", {"start": v(11.8, 75.33) * mm, "end": v(11.8, 51.7) * mm});
            skSolve(sketch);
        }
        {
            var Q0;
            Q0=makeQuery(id+"F28.opExtrude","SWEPT_FACE",FACE,{"disambiguationData":[OSD([sQuery(id+"F20.wireOp",EDGE,"E11.top")])]});
            var sketch = newSketch(context, id + "F72", { "sketchPlane" : qUnion([Q0])});
            skLineSegment(sketch, "E30.bottom", {"start": v(-37.23, 49.87) * mm, "end": v(-13.6, 49.87) * mm});
            skLineSegment(sketch, "E30.top", {"start": v(-37.23, 26.3) * mm, "end": v(-13.6, 26.3) * mm});
            skLineSegment(sketch, "E30.left", {"start": v(-37.23, 49.87) * mm, "end": v(-37.23, 26.3) * mm});
            skLineSegment(sketch, "E30.right", {"start": v(-13.6, 49.87) * mm, "end": v(-13.6, 26.3) * mm});
            skSolve(sketch);
        }
        {
            var Q0;
            Q0=makeQuery(id+"F27.opExtrude","SWEPT_FACE",FACE,{"disambiguationData":[OSD([sQuery(id+"F19.wireOp",EDGE,"E10.top")])]});
            var sketch = newSketch(context, id + "F73", { "sketchPlane" : qUnion([Q0])});
            skLineSegment(sketch, "E31.bottom", {"start": v(-11.82, 49.89) * mm, "end": v(11.8, 49.89) * mm});
            skLineSegment(sketch, "E31.top", {"start": v(-11.82, 26.29) * mm, "end": v(11.8, 26.29) * mm});
            skLineSegment(sketch, "E31.left", {"start": v(-11.82, 49.89) * mm, "end": v(-11.82, 26.29) * mm});
            skLineSegment(sketch, "E31.right", {"start": v(11.8, 49.89) * mm, "end": v(11.8, 26.29) * mm});
            skSolve(sketch);
        }
        {
            var Q0;
            Q0=makeQuery(id+"F26.opExtrude","SWEPT_FACE",FACE,{"disambiguationData":[OSD([sQuery(id+"F18.wireOp",EDGE,"E9.top")])]});
            var sketch = newSketch(context, id + "F74", { "sketchPlane" : qUnion([Q0])});
            skLineSegment(sketch, "E32.bottom", {"start": v(13.57, 49.87) * mm, "end": v(37.2, 49.87) * mm});
            skLineSegment(sketch, "E32.top", {"start": v(13.57, 26.3) * mm, "end": v(37.2, 26.3) * mm});
            skLineSegment(sketch, "E32.left", {"start": v(13.57, 49.87) * mm, "end": v(13.57, 26.3) * mm});
            skLineSegment(sketch, "E32.right", {"start": v(37.2, 49.87) * mm, "end": v(37.2, 26.3) * mm});
            skSolve(sketch);
        }
        {
            var Q0;
            Q0=makeQuery(id+"F10.opExtrude","SWEPT_FACE",FACE,{"disambiguationData":[OSD([sQuery(id+"F2.wireOp",EDGE,"E2.top")])]});
            var sketch = newSketch(context, id + "F75", { "sketchPlane" : qUnion([Q0])});
            skLineSegment(sketch, "E33.bottom", {"start": v(-11.81, 24.49) * mm, "end": v(11.8, 24.49) * mm});
            skLineSegment(sketch, "E33.top", {"start": v(-11.81, 0.9) * mm, "end": v(11.8, 0.9) * mm});
            skLineSegment(sketch, "E33.left", {"start": v(-11.81, 24.49) * mm, "end": v(-11.81, 0.9) * mm});
            skLineSegment(sketch, "E33.right", {"start": v(11.8, 24.49) * mm, "end": v(11.8, 0.9) * mm});
            skSolve(sketch);
        }
        {
            var Q0;
            Q0=makeQuery(id+"F71.imprint","IMPRINT",FACE,{"disambiguationData":[TD([[makeQuery(id+"F71.imprint","IMPRINT",EDGE,{"derivedFrom":sQuery(id+"F71.wireOp",EDGE,"E29.bottom")}),-1.0]])]});
            var Q1;
            Q1=makeQuery(id+"F74.imprint","IMPRINT",FACE,{"disambiguationData":[TD([[makeQuery(id+"F74.imprint","IMPRINT",EDGE,{"derivedFrom":sQuery(id+"F74.wireOp",EDGE,"E32.bottom")}),-1.0]])]});
            var Q2;
            Q2=makeQuery(id+"F72.imprint","IMPRINT",FACE,{"disambiguationData":[TD([[makeQuery(id+"F72.imprint","IMPRINT",EDGE,{"derivedFrom":sQuery(id+"F72.wireOp",EDGE,"E30.bottom")}),-1.0]])]});
            var Q3;
            Q3=makeQuery(id+"F75.imprint","IMPRINT",FACE,{"disambiguationData":[TD([[makeQuery(id+"F75.imprint","IMPRINT",EDGE,{"derivedFrom":sQuery(id+"F75.wireOp",EDGE,"E33.bottom")}),-1.0]])]});
            extrude(context, id + "F76", {"entities" : qUnion([Q0, Q1, Q2, Q3]), "depth" : 12.7 * mm, "offsetDistance" : 25.4 * mm});
        }
        {
            var Q0;
            Q0=makeQuery(id+"F50.opExtrude","SWEPT_FACE",FACE,{"disambiguationData":[OSD([sQuery(id+"F24.wireOp",EDGE,"E15.top")])]});
            var sketch = newSketch(context, id + "F77", { "sketchPlane" : qUnion([Q0])});
            skLineSegment(sketch, "E34.bottom", {"start": v(-11.75, 75.36) * mm, "end": v(11.8, 75.36) * mm});
            skLineSegment(sketch, "E34.top", {"start": v(-11.75, 51.7) * mm, "end": v(11.8, 51.7) * mm});
            skLineSegment(sketch, "E34.left", {"start": v(-11.75, 75.36) * mm, "end": v(-11.75, 51.7) * mm});
            skLineSegment(sketch, "E34.right", {"start": v(11.8, 75.36) * mm, "end": v(11.8, 51.7) * mm});
            skSolve(sketch);
        }
        {
            var Q0;
            Q0=makeQuery(id+"F31.opExtrude","SWEPT_FACE",FACE,{"disambiguationData":[OSD([sQuery(id+"F23.wireOp",EDGE,"E14.top")])]});
            var sketch = newSketch(context, id + "F78", { "sketchPlane" : qUnion([Q0])});
            skLineSegment(sketch, "E35.bottom", {"start": v(-37.24, 49.87) * mm, "end": v(-13.6, 49.87) * mm});
            skLineSegment(sketch, "E35.top", {"start": v(-37.24, 26.29) * mm, "end": v(-13.6, 26.29) * mm});
            skLineSegment(sketch, "E35.left", {"start": v(-37.24, 49.87) * mm, "end": v(-37.24, 26.29) * mm});
            skLineSegment(sketch, "E35.right", {"start": v(-13.6, 49.87) * mm, "end": v(-13.6, 26.29) * mm});
            skSolve(sketch);
        }
        {
            var Q0;
            Q0=makeQuery(id+"F32.opExtrude","SWEPT_FACE",FACE,{"disambiguationData":[OSD([sQuery(id+"F24.wireOp",EDGE,"E15.top")])]});
            var sketch = newSketch(context, id + "F79", { "sketchPlane" : qUnion([Q0])});
            skLineSegment(sketch, "E36.bottom", {"start": v(-11.8, 49.9) * mm, "end": v(11.81, 49.9) * mm});
            skLineSegment(sketch, "E36.top", {"start": v(-11.8, 26.3) * mm, "end": v(11.81, 26.3) * mm});
            skLineSegment(sketch, "E36.left", {"start": v(-11.8, 49.9) * mm, "end": v(-11.8, 26.3) * mm});
            skLineSegment(sketch, "E36.right", {"start": v(11.81, 49.9) * mm, "end": v(11.81, 26.3) * mm});
            skSolve(sketch);
        }
        {
            var Q0;
            Q0=makeQuery(id+"F33.opExtrude","SWEPT_FACE",FACE,{"disambiguationData":[OSD([sQuery(id+"F25.wireOp",EDGE,"E16.top")])]});
            var sketch = newSketch(context, id + "F80", { "sketchPlane" : qUnion([Q0])});
            skLineSegment(sketch, "E37.bottom", {"start": v(13.56, 49.86) * mm, "end": v(37.23, 49.86) * mm});
            skLineSegment(sketch, "E37.top", {"start": v(13.56, 26.33) * mm, "end": v(37.23, 26.33) * mm});
            skLineSegment(sketch, "E37.left", {"start": v(13.56, 49.86) * mm, "end": v(13.56, 26.33) * mm});
            skLineSegment(sketch, "E37.right", {"start": v(37.23, 49.86) * mm, "end": v(37.23, 26.33) * mm});
            skSolve(sketch);
        }
        {
            var Q0;
            Q0=makeQuery(id+"F16.opExtrude","SWEPT_FACE",FACE,{"disambiguationData":[OSD([sQuery(id+"F6.wireOp",EDGE,"E6.top")])]});
            var sketch = newSketch(context, id + "F81", { "sketchPlane" : qUnion([Q0])});
            skLineSegment(sketch, "E38.bottom", {"start": v(-11.78, 24.52) * mm, "end": v(11.82, 24.52) * mm});
            skLineSegment(sketch, "E38.top", {"start": v(-11.78, 0.92) * mm, "end": v(11.82, 0.92) * mm});
            skLineSegment(sketch, "E38.left", {"start": v(-11.78, 24.52) * mm, "end": v(-11.78, 0.92) * mm});
            skLineSegment(sketch, "E38.right", {"start": v(11.82, 24.52) * mm, "end": v(11.82, 0.92) * mm});
            skSolve(sketch);
        }
        {
            var Q0;
            Q0=makeQuery(id+"F52.opExtrude","SWEPT_FACE",FACE,{"disambiguationData":[OSD([sQuery(id+"F22.wireOp",EDGE,"E13.right")])]});
            var sketch = newSketch(context, id + "F82", { "sketchPlane" : qUnion([Q0])});
            skLineSegment(sketch, "E39.bottom", {"start": v(-11.77, 75.33) * mm, "end": v(11.81, 75.33) * mm});
            skLineSegment(sketch, "E39.top", {"start": v(-11.77, 51.7) * mm, "end": v(11.81, 51.7) * mm});
            skLineSegment(sketch, "E39.left", {"start": v(-11.77, 75.33) * mm, "end": v(-11.77, 51.7) * mm});
            skLineSegment(sketch, "E39.right", {"start": v(11.81, 75.33) * mm, "end": v(11.81, 51.7) * mm});
            skSolve(sketch);
        }
        {
            var Q0;
            Q0=makeQuery(id+"F33.opExtrude","SWEPT_FACE",FACE,{"disambiguationData":[OSD([sQuery(id+"F25.wireOp",EDGE,"E16.right")])]});
            var sketch = newSketch(context, id + "F83", { "sketchPlane" : qUnion([Q0])});
            skLineSegment(sketch, "E40.bottom", {"start": v(-37.24, 49.86) * mm, "end": v(-13.6, 49.86) * mm});
            skLineSegment(sketch, "E40.top", {"start": v(-37.24, 26.3) * mm, "end": v(-13.6, 26.3) * mm});
            skLineSegment(sketch, "E40.left", {"start": v(-37.24, 49.86) * mm, "end": v(-37.24, 26.3) * mm});
            skLineSegment(sketch, "E40.right", {"start": v(-13.6, 49.86) * mm, "end": v(-13.6, 26.3) * mm});
            skSolve(sketch);
        }
        {
            var Q0;
            Q0=makeQuery(id+"F30.opExtrude","SWEPT_FACE",FACE,{"disambiguationData":[OSD([sQuery(id+"F22.wireOp",EDGE,"E13.right")])]});
            var sketch = newSketch(context, id + "F84", { "sketchPlane" : qUnion([Q0])});
            skLineSegment(sketch, "E41.bottom", {"start": v(-11.8, 49.9) * mm, "end": v(11.8, 49.9) * mm});
            skLineSegment(sketch, "E41.top", {"start": v(-11.8, 26.3) * mm, "end": v(11.8, 26.3) * mm});
            skLineSegment(sketch, "E41.left", {"start": v(-11.8, 49.9) * mm, "end": v(-11.8, 26.3) * mm});
            skLineSegment(sketch, "E41.right", {"start": v(11.8, 49.9) * mm, "end": v(11.8, 26.3) * mm});
            skSolve(sketch);
        }
        {
            var Q0;
            Q0=makeQuery(id+"F28.opExtrude","SWEPT_FACE",FACE,{"disambiguationData":[OSD([sQuery(id+"F20.wireOp",EDGE,"E11.right")])]});
            var sketch = newSketch(context, id + "F85", { "sketchPlane" : qUnion([Q0])});
            skLineSegment(sketch, "E42.bottom", {"start": v(13.57, 49.87) * mm, "end": v(37.22, 49.87) * mm});
            skLineSegment(sketch, "E42.top", {"start": v(13.57, 26.31) * mm, "end": v(37.22, 26.31) * mm});
            skLineSegment(sketch, "E42.left", {"start": v(13.57, 49.87) * mm, "end": v(13.57, 26.31) * mm});
            skLineSegment(sketch, "E42.right", {"start": v(37.22, 49.87) * mm, "end": v(37.22, 26.31) * mm});
            skSolve(sketch);
        }
        {
            var Q0;
            Q0=makeQuery(id+"F14.opExtrude","SWEPT_FACE",FACE,{"disambiguationData":[OSD([sQuery(id+"F4.wireOp",EDGE,"E4.right")])]});
            var sketch = newSketch(context, id + "F86", { "sketchPlane" : qUnion([Q0])});
            skLineSegment(sketch, "E43.bottom", {"start": v(-11.79, 24.52) * mm, "end": v(11.82, 24.52) * mm});
            skLineSegment(sketch, "E43.top", {"start": v(-11.79, 0.92) * mm, "end": v(11.82, 0.92) * mm});
            skLineSegment(sketch, "E43.left", {"start": v(-11.79, 24.52) * mm, "end": v(-11.79, 0.92) * mm});
            skLineSegment(sketch, "E43.right", {"start": v(11.82, 24.52) * mm, "end": v(11.82, 0.92) * mm});
            skSolve(sketch);
        }
        {
            var Q0;
            Q0=makeQuery(id+"F16.opExtrude","CAP_FACE",FACE,{"disambiguationData":[OSD([sQuery(id+"F6.wireOp",EDGE,"E6.bottom"),sQuery(id+"F6.wireOp",EDGE,"E6.top"),sQuery(id+"F6.wireOp",EDGE,"E6.left"),sQuery(id+"F6.wireOp",EDGE,"E6.right")])],"isStart":true});
            var sketch = newSketch(context, id + "F87", { "sketchPlane" : qUnion([Q0])});
            skLineSegment(sketch, "E44.bottom", {"start": v(-11.8, 37.2) * mm, "end": v(11.8, 37.2) * mm});
            skLineSegment(sketch, "E44.top", {"start": v(-11.8, 13.6) * mm, "end": v(11.8, 13.6) * mm});
            skLineSegment(sketch, "E44.left", {"start": v(-11.8, 37.2) * mm, "end": v(-11.8, 13.6) * mm});
            skLineSegment(sketch, "E44.right", {"start": v(11.8, 37.2) * mm, "end": v(11.8, 13.6) * mm});
            skSolve(sketch);
        }
        {
            var Q0;
            Q0=makeQuery(id+"F12.opExtrude","CAP_FACE",FACE,{"disambiguationData":[OSD([sQuery(id+"F7.wireOp",EDGE,"E7.bottom"),sQuery(id+"F7.wireOp",EDGE,"E7.top"),sQuery(id+"F7.wireOp",EDGE,"E7.left"),sQuery(id+"F7.wireOp",EDGE,"E7.right")])],"isStart":true});
            var sketch = newSketch(context, id + "F88", { "sketchPlane" : qUnion([Q0])});
            skLineSegment(sketch, "E45.bottom", {"start": v(-37.21, 11.8) * mm, "end": v(-13.6, 11.8) * mm});
            skLineSegment(sketch, "E45.top", {"start": v(-37.21, -11.8) * mm, "end": v(-13.6, -11.8) * mm});
            skLineSegment(sketch, "E45.left", {"start": v(-37.21, 11.8) * mm, "end": v(-37.21, -11.8) * mm});
            skLineSegment(sketch, "E45.right", {"start": v(-13.6, 11.8) * mm, "end": v(-13.6, -11.8) * mm});
            skSolve(sketch);
        }
        {
            var Q0;
            Q0=makeQuery(id+"F13.opExtrude","CAP_FACE",FACE,{"disambiguationData":[OSD([sQuery(id+"F0.wireOp",EDGE,"E0.bottom"),sQuery(id+"F0.wireOp",EDGE,"E0.top"),sQuery(id+"F0.wireOp",EDGE,"E0.left"),sQuery(id+"F0.wireOp",EDGE,"E0.right")])],"isStart":true});
            var sketch = newSketch(context, id + "F89", { "sketchPlane" : qUnion([Q0])});
            skLineSegment(sketch, "E46.bottom", {"start": v(-11.83, 11.78) * mm, "end": v(11.81, 11.78) * mm});
            skLineSegment(sketch, "E46.top", {"start": v(-11.83, -11.8) * mm, "end": v(11.81, -11.8) * mm});
            skLineSegment(sketch, "E46.left", {"start": v(-11.83, 11.78) * mm, "end": v(-11.83, -11.8) * mm});
            skLineSegment(sketch, "E46.right", {"start": v(11.81, 11.78) * mm, "end": v(11.81, -11.8) * mm});
            skSolve(sketch);
        }
        {
            var Q0;
            Q0=makeQuery(id+"F14.opExtrude","CAP_FACE",FACE,{"disambiguationData":[OSD([sQuery(id+"F4.wireOp",EDGE,"E4.bottom"),sQuery(id+"F4.wireOp",EDGE,"E4.top"),sQuery(id+"F4.wireOp",EDGE,"E4.left"),sQuery(id+"F4.wireOp",EDGE,"E4.right")])],"isStart":true});
            var sketch = newSketch(context, id + "F90", { "sketchPlane" : qUnion([Q0])});
            skLineSegment(sketch, "E47.bottom", {"start": v(13.6, 11.81) * mm, "end": v(37.2, 11.81) * mm});
            skLineSegment(sketch, "E47.top", {"start": v(13.6, -11.8) * mm, "end": v(37.2, -11.8) * mm});
            skLineSegment(sketch, "E47.left", {"start": v(13.6, 11.81) * mm, "end": v(13.6, -11.8) * mm});
            skLineSegment(sketch, "E47.right", {"start": v(37.2, 11.81) * mm, "end": v(37.2, -11.8) * mm});
            skSolve(sketch);
        }
        {
            var Q0;
            Q0=makeQuery(id+"F10.opExtrude","CAP_FACE",FACE,{"disambiguationData":[OSD([sQuery(id+"F2.wireOp",EDGE,"E2.bottom"),sQuery(id+"F2.wireOp",EDGE,"E2.top"),sQuery(id+"F2.wireOp",EDGE,"E2.left"),sQuery(id+"F2.wireOp",EDGE,"E2.right")])],"isStart":true});
            var sketch = newSketch(context, id + "F91", { "sketchPlane" : qUnion([Q0])});
            skLineSegment(sketch, "E48.bottom", {"start": v(-11.84, -13.63) * mm, "end": v(11.8, -13.63) * mm});
            skLineSegment(sketch, "E48.top", {"start": v(-11.84, -37.2) * mm, "end": v(11.8, -37.2) * mm});
            skLineSegment(sketch, "E48.left", {"start": v(-11.84, -13.63) * mm, "end": v(-11.84, -37.2) * mm});
            skLineSegment(sketch, "E48.right", {"start": v(11.8, -13.63) * mm, "end": v(11.8, -37.2) * mm});
            skSolve(sketch);
        }
        {
            var Q0;
            Q0=makeQuery(id+"F87.imprint","IMPRINT",FACE,{"disambiguationData":[TD([[makeQuery(id+"F87.imprint","IMPRINT",EDGE,{"derivedFrom":sQuery(id+"F87.wireOp",EDGE,"E44.bottom")}),-1.0]])]});
            var Q1;
            Q1=makeQuery(id+"F90.imprint","IMPRINT",FACE,{"disambiguationData":[TD([[makeQuery(id+"F90.imprint","IMPRINT",EDGE,{"derivedFrom":sQuery(id+"F90.wireOp",EDGE,"E47.bottom")}),-1.0]])]});
            var Q2;
            Q2=makeQuery(id+"F88.imprint","IMPRINT",FACE,{"disambiguationData":[TD([[makeQuery(id+"F88.imprint","IMPRINT",EDGE,{"derivedFrom":sQuery(id+"F88.wireOp",EDGE,"E45.bottom")}),-1.0]])]});
            var Q3;
            Q3=makeQuery(id+"F91.imprint","IMPRINT",FACE,{"disambiguationData":[TD([[makeQuery(id+"F91.imprint","IMPRINT",EDGE,{"derivedFrom":sQuery(id+"F91.wireOp",EDGE,"E48.bottom")}),-1.0]])]});
            extrude(context, id + "F92", {"entities" : qUnion([Q0, Q1, Q2, Q3]), "depth" : 12.7 * mm, "offsetDistance" : 25.4 * mm});
        }
        {
            var Q0;
            Q0=makeQuery(id+"F77.imprint","IMPRINT",FACE,{"disambiguationData":[TD([[makeQuery(id+"F77.imprint","IMPRINT",EDGE,{"derivedFrom":sQuery(id+"F77.wireOp",EDGE,"E34.bottom")}),-1.0]])]});
            var Q1;
            Q1=makeQuery(id+"F80.imprint","IMPRINT",FACE,{"disambiguationData":[TD([[makeQuery(id+"F80.imprint","IMPRINT",EDGE,{"derivedFrom":sQuery(id+"F80.wireOp",EDGE,"E37.bottom")}),-1.0]])]});
            var Q2;
            Q2=makeQuery(id+"F78.imprint","IMPRINT",FACE,{"disambiguationData":[TD([[makeQuery(id+"F78.imprint","IMPRINT",EDGE,{"derivedFrom":sQuery(id+"F78.wireOp",EDGE,"E35.bottom")}),-1.0]])]});
            var Q3;
            Q3=makeQuery(id+"F81.imprint","IMPRINT",FACE,{"disambiguationData":[TD([[makeQuery(id+"F81.imprint","IMPRINT",EDGE,{"derivedFrom":sQuery(id+"F81.wireOp",EDGE,"E38.bottom")}),-1.0]])]});
            extrude(context, id + "F93", {"entities" : qUnion([Q0, Q1, Q2, Q3]), "depth" : 12.7 * mm, "offsetDistance" : 25.4 * mm});
        }
        {
            var Q0;
            Q0=makeQuery(id+"F82.imprint","IMPRINT",FACE,{"disambiguationData":[TD([[makeQuery(id+"F82.imprint","IMPRINT",EDGE,{"derivedFrom":sQuery(id+"F82.wireOp",EDGE,"E39.bottom")}),-1.0]])]});
            var Q1;
            Q1=makeQuery(id+"F85.imprint","IMPRINT",FACE,{"disambiguationData":[TD([[makeQuery(id+"F85.imprint","IMPRINT",EDGE,{"derivedFrom":sQuery(id+"F85.wireOp",EDGE,"E42.bottom")}),-1.0]])]});
            var Q2;
            Q2=makeQuery(id+"F83.imprint","IMPRINT",FACE,{"disambiguationData":[TD([[makeQuery(id+"F83.imprint","IMPRINT",EDGE,{"derivedFrom":sQuery(id+"F83.wireOp",EDGE,"E40.bottom")}),-1.0]])]});
            var Q3;
            Q3=makeQuery(id+"F86.imprint","IMPRINT",FACE,{"disambiguationData":[TD([[makeQuery(id+"F86.imprint","IMPRINT",EDGE,{"derivedFrom":sQuery(id+"F86.wireOp",EDGE,"E43.bottom")}),-1.0]])]});
            extrude(context, id + "F94", {"entities" : qUnion([Q0, Q1, Q2, Q3]), "depth" : 12.7 * mm, "offsetDistance" : 25.4 * mm});
        }
        {
            var Q0;
            Q0=makeQuery(id+"F92.opExtrude","SWEPT_EDGE",EDGE,{"disambiguationData":[OSD([sQuery(id+"F89.wireOp",EDGE,"E46.bottom"),sQuery(id+"F89.wireOp",EDGE,"E46.left")])]});
            var Q1;
            Q1=makeQuery(id+"F92.opExtrude","SWEPT_EDGE",EDGE,{"disambiguationData":[OSD([sQuery(id+"F89.wireOp",EDGE,"E46.bottom"),sQuery(id+"F89.wireOp",EDGE,"E46.right")])]});
            var Q2;
            Q2=makeQuery(id+"F92.opExtrude","SWEPT_EDGE",EDGE,{"disambiguationData":[OSD([sQuery(id+"F89.wireOp",EDGE,"E46.top"),sQuery(id+"F89.wireOp",EDGE,"E46.right")])]});
            var Q3;
            Q3=makeQuery(id+"F92.opExtrude","SWEPT_EDGE",EDGE,{"disambiguationData":[OSD([sQuery(id+"F89.wireOp",EDGE,"E46.top"),sQuery(id+"F89.wireOp",EDGE,"E46.left")])]});
            var Q4;
            Q4=makeQuery(id+"F70.opExtrude","SWEPT_EDGE",EDGE,{"disambiguationData":[OSD([sQuery(id+"F67.wireOp",EDGE,"E26.top"),sQuery(id+"F67.wireOp",EDGE,"E26.left")])]});
            var Q5;
            Q5=makeQuery(id+"F70.opExtrude","SWEPT_EDGE",EDGE,{"disambiguationData":[OSD([sQuery(id+"F67.wireOp",EDGE,"E26.top"),sQuery(id+"F67.wireOp",EDGE,"E26.right")])]});
            var Q6;
            Q6=makeQuery(id+"F70.opExtrude","SWEPT_EDGE",EDGE,{"disambiguationData":[OSD([sQuery(id+"F67.wireOp",EDGE,"E26.bottom"),sQuery(id+"F67.wireOp",EDGE,"E26.left")])]});
            var Q7;
            Q7=makeQuery(id+"F70.opExtrude","SWEPT_EDGE",EDGE,{"disambiguationData":[OSD([sQuery(id+"F67.wireOp",EDGE,"E26.bottom"),sQuery(id+"F67.wireOp",EDGE,"E26.right")])]});
            var Q8;
            Q8=makeQuery(id+"F93.opExtrude","SWEPT_EDGE",EDGE,{"disambiguationData":[OSD([sQuery(id+"F79.wireOp",EDGE,"E36.bottom"),sQuery(id+"F79.wireOp",EDGE,"E36.left")])]});
            var Q9;
            Q9=makeQuery(id+"F93.opExtrude","SWEPT_EDGE",EDGE,{"disambiguationData":[OSD([sQuery(id+"F79.wireOp",EDGE,"E36.top"),sQuery(id+"F79.wireOp",EDGE,"E36.left")])]});
            var Q10;
            Q10=makeQuery(id+"F93.opExtrude","SWEPT_EDGE",EDGE,{"disambiguationData":[OSD([sQuery(id+"F79.wireOp",EDGE,"E36.top"),sQuery(id+"F79.wireOp",EDGE,"E36.right")])]});
            var Q11;
            Q11=makeQuery(id+"F93.opExtrude","SWEPT_EDGE",EDGE,{"disambiguationData":[OSD([sQuery(id+"F79.wireOp",EDGE,"E36.bottom"),sQuery(id+"F79.wireOp",EDGE,"E36.right")])]});
            var Q12;
            Q12=makeQuery(id+"F76.opExtrude","SWEPT_EDGE",EDGE,{"disambiguationData":[OSD([sQuery(id+"F73.wireOp",EDGE,"E31.bottom"),sQuery(id+"F73.wireOp",EDGE,"E31.right")])]});
            var Q13;
            Q13=makeQuery(id+"F76.opExtrude","SWEPT_EDGE",EDGE,{"disambiguationData":[OSD([sQuery(id+"F73.wireOp",EDGE,"E31.top"),sQuery(id+"F73.wireOp",EDGE,"E31.right")])]});
            var Q14;
            Q14=makeQuery(id+"F76.opExtrude","SWEPT_EDGE",EDGE,{"disambiguationData":[OSD([sQuery(id+"F73.wireOp",EDGE,"E31.top"),sQuery(id+"F73.wireOp",EDGE,"E31.left")])]});
            var Q15;
            Q15=makeQuery(id+"F76.opExtrude","SWEPT_EDGE",EDGE,{"disambiguationData":[OSD([sQuery(id+"F73.wireOp",EDGE,"E31.bottom"),sQuery(id+"F73.wireOp",EDGE,"E31.left")])]});
            var Q16;
            Q16=makeQuery(id+"F64.opExtrude","SWEPT_EDGE",EDGE,{"disambiguationData":[OSD([sQuery(id+"F57.wireOp",EDGE,"E20.bottom"),sQuery(id+"F57.wireOp",EDGE,"E20.right")])]});
            var Q17;
            Q17=makeQuery(id+"F64.opExtrude","SWEPT_EDGE",EDGE,{"disambiguationData":[OSD([sQuery(id+"F57.wireOp",EDGE,"E20.top"),sQuery(id+"F57.wireOp",EDGE,"E20.right")])]});
            var Q18;
            Q18=makeQuery(id+"F64.opExtrude","SWEPT_EDGE",EDGE,{"disambiguationData":[OSD([sQuery(id+"F57.wireOp",EDGE,"E20.top"),sQuery(id+"F57.wireOp",EDGE,"E20.left")])]});
            var Q19;
            Q19=makeQuery(id+"F64.opExtrude","SWEPT_EDGE",EDGE,{"disambiguationData":[OSD([sQuery(id+"F57.wireOp",EDGE,"E20.bottom"),sQuery(id+"F57.wireOp",EDGE,"E20.left")])]});
            var Q20;
            Q20=makeQuery(id+"F94.opExtrude","SWEPT_EDGE",EDGE,{"disambiguationData":[OSD([sQuery(id+"F84.wireOp",EDGE,"E41.bottom"),sQuery(id+"F84.wireOp",EDGE,"E41.left")])]});
            var Q21;
            Q21=makeQuery(id+"F94.opExtrude","SWEPT_EDGE",EDGE,{"disambiguationData":[OSD([sQuery(id+"F84.wireOp",EDGE,"E41.bottom"),sQuery(id+"F84.wireOp",EDGE,"E41.right")])]});
            var Q22;
            Q22=makeQuery(id+"F94.opExtrude","SWEPT_EDGE",EDGE,{"disambiguationData":[OSD([sQuery(id+"F84.wireOp",EDGE,"E41.top"),sQuery(id+"F84.wireOp",EDGE,"E41.right")])]});
            var Q23;
            Q23=makeQuery(id+"F94.opExtrude","SWEPT_EDGE",EDGE,{"disambiguationData":[OSD([sQuery(id+"F84.wireOp",EDGE,"E41.top"),sQuery(id+"F84.wireOp",EDGE,"E41.left")])]});
            fillet(context, id + "F95", {"entities" : qUnion([Q0, Q1, Q2, Q3, Q4, Q5, Q6, Q7, Q8, Q9, Q10, Q11, Q12, Q13, Q14, Q15, Q16, Q17, Q18, Q19, Q20, Q21, Q22, Q23]), "radius" : 7.62 * mm, "tangentPropagation" : true, "rho" : 0.5, "crossSection" : FilletCrossSection.CONIC, "allowEdgeOverflow" : false});
        }
        {
            var Q0;
            Q0=makeQuery(id+"F76.opExtrude","SWEPT_EDGE",EDGE,{"disambiguationData":[OSD([sQuery(id+"F71.wireOp",EDGE,"E29.top"),sQuery(id+"F71.wireOp",EDGE,"E29.left")])]});
            var Q1;
            Q1=makeQuery(id+"F76.opExtrude","SWEPT_EDGE",EDGE,{"disambiguationData":[OSD([sQuery(id+"F71.wireOp",EDGE,"E29.top"),sQuery(id+"F71.wireOp",EDGE,"E29.right")])]});
            chamfer(context, id + "F96", {"entities" : qUnion([Q0, Q1]), "width" : 5.08 * mm, "tangentPropagation" : true});
        }
        {
            var Q0;
            {var subQ0=sQuery(id+"F71.wireOp",EDGE,"E29.top");Q0=makeQuery(id+"F96.opChamfer","BLEND_EDGE",EDGE,{"blendedFrom":[makeQuery(id+"F76.opExtrude","SWEPT_EDGE",EDGE,{"disambiguationData":[OSD([subQ0,sQuery(id+"F71.wireOp",EDGE,"E29.left")])]}),makeQuery(id+"F76.opExtrude","SWEPT_FACE",FACE,{"disambiguationData":[OSD([subQ0])]})],"blendedInto":[makeQuery(id+"F76.opExtrude","SWEPT_FACE",FACE,{"disambiguationData":[OSD([subQ0])]})]});}
            var Q1;
            {var subQ0=sQuery(id+"F71.wireOp",EDGE,"E29.top");Q1=makeQuery(id+"F96.opChamfer","BLEND_EDGE",EDGE,{"blendedFrom":[makeQuery(id+"F76.opExtrude","SWEPT_EDGE",EDGE,{"disambiguationData":[OSD([subQ0,sQuery(id+"F71.wireOp",EDGE,"E29.right")])]}),makeQuery(id+"F76.opExtrude","SWEPT_FACE",FACE,{"disambiguationData":[OSD([subQ0])]})],"blendedInto":[makeQuery(id+"F76.opExtrude","SWEPT_FACE",FACE,{"disambiguationData":[OSD([subQ0])]})]});}
            fillet(context, id + "F97", {"entities" : qUnion([Q0, Q1]), "radius" : 35.56 * mm, "tangentPropagation" : true, "allowEdgeOverflow" : false});
        }
        {
            var Q0;
            {var subQ0=sQuery(id+"F71.wireOp",EDGE,"E29.top");var subQ1=makeQuery(id+"F76.opExtrude","SWEPT_FACE",FACE,{"disambiguationData":[OSD([subQ0])]});Q0=makeQuery(id+"F97.opFillet","BLEND_EDGE",EDGE,{"blendedFrom":[makeQuery(id+"F96.opChamfer","BLEND_EDGE",EDGE,{"blendedFrom":[makeQuery(id+"F76.opExtrude","SWEPT_EDGE",EDGE,{"disambiguationData":[OSD([subQ0,sQuery(id+"F71.wireOp",EDGE,"E29.left")])]}),subQ1],"blendedInto":[subQ1]}),makeQuery(id+"F96.opChamfer","BLEND_EDGE",EDGE,{"blendedFrom":[makeQuery(id+"F76.opExtrude","SWEPT_EDGE",EDGE,{"disambiguationData":[OSD([subQ0,sQuery(id+"F71.wireOp",EDGE,"E29.right")])]}),subQ1],"blendedInto":[subQ1]})],"blendedInto":[]});}
            fillet(context, id + "F98", {"entities" : qUnion([Q0]), "radius" : 25.4 * mm, "tangentPropagation" : true, "allowEdgeOverflow" : false});
        }
        {
            var Q0;
            Q0=makeQuery(id+"F76.opExtrude","SWEPT_EDGE",EDGE,{"disambiguationData":[OSD([sQuery(id+"F72.wireOp",EDGE,"E30.top"),sQuery(id+"F72.wireOp",EDGE,"E30.right")])]});
            var Q1;
            Q1=makeQuery(id+"F76.opExtrude","SWEPT_EDGE",EDGE,{"disambiguationData":[OSD([sQuery(id+"F72.wireOp",EDGE,"E30.bottom"),sQuery(id+"F72.wireOp",EDGE,"E30.right")])]});
            var Q2;
            Q2=makeQuery(id+"F76.opExtrude","SWEPT_EDGE",EDGE,{"disambiguationData":[OSD([sQuery(id+"F75.wireOp",EDGE,"E33.bottom"),sQuery(id+"F75.wireOp",EDGE,"E33.right")])]});
            var Q3;
            Q3=makeQuery(id+"F76.opExtrude","SWEPT_EDGE",EDGE,{"disambiguationData":[OSD([sQuery(id+"F75.wireOp",EDGE,"E33.bottom"),sQuery(id+"F75.wireOp",EDGE,"E33.left")])]});
            var Q4;
            Q4=makeQuery(id+"F76.opExtrude","SWEPT_EDGE",EDGE,{"disambiguationData":[OSD([sQuery(id+"F74.wireOp",EDGE,"E32.bottom"),sQuery(id+"F74.wireOp",EDGE,"E32.left")])]});
            var Q5;
            Q5=makeQuery(id+"F76.opExtrude","SWEPT_EDGE",EDGE,{"disambiguationData":[OSD([sQuery(id+"F74.wireOp",EDGE,"E32.top"),sQuery(id+"F74.wireOp",EDGE,"E32.left")])]});
            var Q6;
            Q6=makeQuery(id+"F64.opExtrude","SWEPT_EDGE",EDGE,{"disambiguationData":[OSD([sQuery(id+"F56.wireOp",EDGE,"E19.top"),sQuery(id+"F56.wireOp",EDGE,"E19.right")])]});
            var Q7;
            Q7=makeQuery(id+"F64.opExtrude","SWEPT_EDGE",EDGE,{"disambiguationData":[OSD([sQuery(id+"F56.wireOp",EDGE,"E19.top"),sQuery(id+"F56.wireOp",EDGE,"E19.left")])]});
            var Q8;
            Q8=makeQuery(id+"F64.opExtrude","SWEPT_EDGE",EDGE,{"disambiguationData":[OSD([sQuery(id+"F60.wireOp",EDGE,"E23.bottom"),sQuery(id+"F60.wireOp",EDGE,"E23.left")])]});
            var Q9;
            Q9=makeQuery(id+"F64.opExtrude","SWEPT_EDGE",EDGE,{"disambiguationData":[OSD([sQuery(id+"F60.wireOp",EDGE,"E23.top"),sQuery(id+"F60.wireOp",EDGE,"E23.left")])]});
            var Q10;
            Q10=makeQuery(id+"F64.opExtrude","SWEPT_EDGE",EDGE,{"disambiguationData":[OSD([sQuery(id+"F54.wireOp",EDGE,"E17.top"),sQuery(id+"F54.wireOp",EDGE,"E17.right")])]});
            var Q11;
            Q11=makeQuery(id+"F64.opExtrude","SWEPT_EDGE",EDGE,{"disambiguationData":[OSD([sQuery(id+"F58.wireOp",EDGE,"E21.bottom"),sQuery(id+"F58.wireOp",EDGE,"E21.left")])]});
            var Q12;
            Q12=makeQuery(id+"F64.opExtrude","SWEPT_EDGE",EDGE,{"disambiguationData":[OSD([sQuery(id+"F54.wireOp",EDGE,"E17.bottom"),sQuery(id+"F54.wireOp",EDGE,"E17.right")])]});
            var Q13;
            Q13=makeQuery(id+"F64.opExtrude","SWEPT_EDGE",EDGE,{"disambiguationData":[OSD([sQuery(id+"F58.wireOp",EDGE,"E21.bottom"),sQuery(id+"F58.wireOp",EDGE,"E21.right")])]});
            var Q14;
            Q14=makeQuery(id+"F93.opExtrude","SWEPT_EDGE",EDGE,{"disambiguationData":[OSD([sQuery(id+"F77.wireOp",EDGE,"E34.top"),sQuery(id+"F77.wireOp",EDGE,"E34.right")])]});
            var Q15;
            Q15=makeQuery(id+"F93.opExtrude","SWEPT_EDGE",EDGE,{"disambiguationData":[OSD([sQuery(id+"F77.wireOp",EDGE,"E34.top"),sQuery(id+"F77.wireOp",EDGE,"E34.left")])]});
            var Q16;
            Q16=makeQuery(id+"F93.opExtrude","SWEPT_EDGE",EDGE,{"disambiguationData":[OSD([sQuery(id+"F78.wireOp",EDGE,"E35.bottom"),sQuery(id+"F78.wireOp",EDGE,"E35.right")])]});
            var Q17;
            Q17=makeQuery(id+"F93.opExtrude","SWEPT_EDGE",EDGE,{"disambiguationData":[OSD([sQuery(id+"F78.wireOp",EDGE,"E35.top"),sQuery(id+"F78.wireOp",EDGE,"E35.right")])]});
            var Q18;
            Q18=makeQuery(id+"F93.opExtrude","SWEPT_EDGE",EDGE,{"disambiguationData":[OSD([sQuery(id+"F81.wireOp",EDGE,"E38.bottom"),sQuery(id+"F81.wireOp",EDGE,"E38.left")])]});
            var Q19;
            Q19=makeQuery(id+"F93.opExtrude","SWEPT_EDGE",EDGE,{"disambiguationData":[OSD([sQuery(id+"F81.wireOp",EDGE,"E38.bottom"),sQuery(id+"F81.wireOp",EDGE,"E38.right")])]});
            var Q20;
            Q20=makeQuery(id+"F93.opExtrude","SWEPT_EDGE",EDGE,{"disambiguationData":[OSD([sQuery(id+"F80.wireOp",EDGE,"E37.bottom"),sQuery(id+"F80.wireOp",EDGE,"E37.left")])]});
            var Q21;
            Q21=makeQuery(id+"F17.opExtrude","SWEPT_FACE",FACE,{"disambiguationData":[OSD([sQuery(id+"F5.wireOp",EDGE,"E5.top")])]});
            var Q22;
            Q22=makeQuery(id+"F93.opExtrude","SWEPT_EDGE",EDGE,{"disambiguationData":[OSD([sQuery(id+"F80.wireOp",EDGE,"E37.top"),sQuery(id+"F80.wireOp",EDGE,"E37.left")])]});
            var Q23;
            Q23=makeQuery(id+"F92.opExtrude","SWEPT_EDGE",EDGE,{"disambiguationData":[OSD([sQuery(id+"F87.wireOp",EDGE,"E44.top"),sQuery(id+"F87.wireOp",EDGE,"E44.left")])]});
            var Q24;
            Q24=makeQuery(id+"F92.opExtrude","SWEPT_EDGE",EDGE,{"disambiguationData":[OSD([sQuery(id+"F87.wireOp",EDGE,"E44.top"),sQuery(id+"F87.wireOp",EDGE,"E44.right")])]});
            var Q25;
            Q25=makeQuery(id+"F92.opExtrude","SWEPT_EDGE",EDGE,{"disambiguationData":[OSD([sQuery(id+"F90.wireOp",EDGE,"E47.bottom"),sQuery(id+"F90.wireOp",EDGE,"E47.left")])]});
            var Q26;
            Q26=makeQuery(id+"F92.opExtrude","SWEPT_EDGE",EDGE,{"disambiguationData":[OSD([sQuery(id+"F90.wireOp",EDGE,"E47.top"),sQuery(id+"F90.wireOp",EDGE,"E47.left")])]});
            var Q27;
            Q27=makeQuery(id+"F92.opExtrude","SWEPT_EDGE",EDGE,{"disambiguationData":[OSD([sQuery(id+"F91.wireOp",EDGE,"E48.bottom"),sQuery(id+"F91.wireOp",EDGE,"E48.left")])]});
            var Q28;
            Q28=makeQuery(id+"F92.opExtrude","SWEPT_EDGE",EDGE,{"disambiguationData":[OSD([sQuery(id+"F88.wireOp",EDGE,"E45.top"),sQuery(id+"F88.wireOp",EDGE,"E45.right")])]});
            var Q29;
            Q29=makeQuery(id+"F92.opExtrude","SWEPT_EDGE",EDGE,{"disambiguationData":[OSD([sQuery(id+"F91.wireOp",EDGE,"E48.bottom"),sQuery(id+"F91.wireOp",EDGE,"E48.right")])]});
            var Q30;
            Q30=makeQuery(id+"F92.opExtrude","SWEPT_EDGE",EDGE,{"disambiguationData":[OSD([sQuery(id+"F88.wireOp",EDGE,"E45.bottom"),sQuery(id+"F88.wireOp",EDGE,"E45.right")])]});
            var Q31;
            Q31=makeQuery(id+"F70.opExtrude","SWEPT_EDGE",EDGE,{"disambiguationData":[OSD([sQuery(id+"F69.wireOp",EDGE,"E28.bottom"),sQuery(id+"F69.wireOp",EDGE,"E28.left")])]});
            var Q32;
            Q32=makeQuery(id+"F70.opExtrude","SWEPT_EDGE",EDGE,{"disambiguationData":[OSD([sQuery(id+"F69.wireOp",EDGE,"E28.top"),sQuery(id+"F69.wireOp",EDGE,"E28.left")])]});
            var Q33;
            Q33=makeQuery(id+"F70.opExtrude","SWEPT_EDGE",EDGE,{"disambiguationData":[OSD([sQuery(id+"F66.wireOp",EDGE,"E25.top"),sQuery(id+"F66.wireOp",EDGE,"E25.left")])]});
            var Q34;
            Q34=makeQuery(id+"F70.opExtrude","SWEPT_EDGE",EDGE,{"disambiguationData":[OSD([sQuery(id+"F66.wireOp",EDGE,"E25.top"),sQuery(id+"F66.wireOp",EDGE,"E25.right")])]});
            var Q35;
            Q35=makeQuery(id+"F70.opExtrude","SWEPT_EDGE",EDGE,{"disambiguationData":[OSD([sQuery(id+"F65.wireOp",EDGE,"E24.bottom"),sQuery(id+"F65.wireOp",EDGE,"E24.right")])]});
            var Q36;
            Q36=makeQuery(id+"F70.opExtrude","SWEPT_EDGE",EDGE,{"disambiguationData":[OSD([sQuery(id+"F65.wireOp",EDGE,"E24.top"),sQuery(id+"F65.wireOp",EDGE,"E24.right")])]});
            var Q37;
            Q37=makeQuery(id+"F70.opExtrude","SWEPT_EDGE",EDGE,{"disambiguationData":[OSD([sQuery(id+"F68.wireOp",EDGE,"E27.bottom"),sQuery(id+"F68.wireOp",EDGE,"E27.left")])]});
            var Q38;
            Q38=makeQuery(id+"F70.opExtrude","SWEPT_EDGE",EDGE,{"disambiguationData":[OSD([sQuery(id+"F68.wireOp",EDGE,"E27.bottom"),sQuery(id+"F68.wireOp",EDGE,"E27.right")])]});
            var Q39;
            Q39=makeQuery(id+"F94.opExtrude","SWEPT_EDGE",EDGE,{"disambiguationData":[OSD([sQuery(id+"F83.wireOp",EDGE,"E40.top"),sQuery(id+"F83.wireOp",EDGE,"E40.right")])]});
            var Q40;
            Q40=makeQuery(id+"F94.opExtrude","SWEPT_EDGE",EDGE,{"disambiguationData":[OSD([sQuery(id+"F86.wireOp",EDGE,"E43.bottom"),sQuery(id+"F86.wireOp",EDGE,"E43.right")])]});
            var Q41;
            Q41=makeQuery(id+"F94.opExtrude","SWEPT_EDGE",EDGE,{"disambiguationData":[OSD([sQuery(id+"F86.wireOp",EDGE,"E43.bottom"),sQuery(id+"F86.wireOp",EDGE,"E43.left")])]});
            var Q42;
            Q42=makeQuery(id+"F94.opExtrude","SWEPT_EDGE",EDGE,{"disambiguationData":[OSD([sQuery(id+"F85.wireOp",EDGE,"E42.top"),sQuery(id+"F85.wireOp",EDGE,"E42.left")])]});
            var Q43;
            Q43=makeQuery(id+"F94.opExtrude","SWEPT_EDGE",EDGE,{"disambiguationData":[OSD([sQuery(id+"F85.wireOp",EDGE,"E42.bottom"),sQuery(id+"F85.wireOp",EDGE,"E42.left")])]});
            var Q44;
            Q44=makeQuery(id+"F94.opExtrude","SWEPT_EDGE",EDGE,{"disambiguationData":[OSD([sQuery(id+"F82.wireOp",EDGE,"E39.top"),sQuery(id+"F82.wireOp",EDGE,"E39.right")])]});
            var Q45;
            Q45=makeQuery(id+"F94.opExtrude","SWEPT_EDGE",EDGE,{"disambiguationData":[OSD([sQuery(id+"F82.wireOp",EDGE,"E39.top"),sQuery(id+"F82.wireOp",EDGE,"E39.left")])]});
            chamfer(context, id + "F99", {"entities" : qUnion([Q0, Q1, Q2, Q3, Q4, Q5, Q6, Q7, Q8, Q9, Q10, Q11, Q12, Q13, Q14, Q15, Q16, Q17, Q18, Q19, Q20, Q21, Q22, Q23, Q24, Q25, Q26, Q27, Q28, Q29, Q30, Q31, Q32, Q33, Q34, Q35, Q36, Q37, Q38, Q39, Q40, Q41, Q42, Q43, Q44, Q45]), "width" : 5.08 * mm, "tangentPropagation" : true});
        }
        {
            var Q0;
            Q0=makeQuery(id+"F94.opExtrude","SWEPT_EDGE",EDGE,{"disambiguationData":[OSD([sQuery(id+"F83.wireOp",EDGE,"E40.bottom"),sQuery(id+"F83.wireOp",EDGE,"E40.right")])]});
            chamfer(context, id + "F100", {"entities" : qUnion([Q0]), "width" : 5.08 * mm, "tangentPropagation" : true});
        }
        {
            var Q0;
            {var subQ0=sQuery(id+"F86.wireOp",EDGE,"E43.bottom");Q0=makeQuery(id+"F99.opChamfer","BLEND_EDGE",EDGE,{"blendedFrom":[makeQuery(id+"F94.opExtrude","SWEPT_EDGE",EDGE,{"disambiguationData":[OSD([subQ0,sQuery(id+"F86.wireOp",EDGE,"E43.right")])]}),makeQuery(id+"F94.opExtrude","SWEPT_FACE",FACE,{"disambiguationData":[OSD([subQ0])]})],"blendedInto":[makeQuery(id+"F94.opExtrude","SWEPT_FACE",FACE,{"disambiguationData":[OSD([subQ0])]})]});}
            var Q1;
            {var subQ0=sQuery(id+"F86.wireOp",EDGE,"E43.bottom");Q1=makeQuery(id+"F99.opChamfer","BLEND_EDGE",EDGE,{"blendedFrom":[makeQuery(id+"F94.opExtrude","SWEPT_EDGE",EDGE,{"disambiguationData":[OSD([subQ0,sQuery(id+"F86.wireOp",EDGE,"E43.left")])]}),makeQuery(id+"F94.opExtrude","SWEPT_FACE",FACE,{"disambiguationData":[OSD([subQ0])]})],"blendedInto":[makeQuery(id+"F94.opExtrude","SWEPT_FACE",FACE,{"disambiguationData":[OSD([subQ0])]})]});}
            var Q2;
            {var subQ0=sQuery(id+"F85.wireOp",EDGE,"E42.left");Q2=makeQuery(id+"F99.opChamfer","BLEND_EDGE",EDGE,{"blendedFrom":[makeQuery(id+"F94.opExtrude","SWEPT_EDGE",EDGE,{"disambiguationData":[OSD([sQuery(id+"F85.wireOp",EDGE,"E42.top"),subQ0])]}),makeQuery(id+"F94.opExtrude","SWEPT_FACE",FACE,{"disambiguationData":[OSD([subQ0])]})],"blendedInto":[makeQuery(id+"F94.opExtrude","SWEPT_FACE",FACE,{"disambiguationData":[OSD([subQ0])]})]});}
            var Q3;
            {var subQ0=sQuery(id+"F85.wireOp",EDGE,"E42.left");Q3=makeQuery(id+"F99.opChamfer","BLEND_EDGE",EDGE,{"blendedFrom":[makeQuery(id+"F94.opExtrude","SWEPT_EDGE",EDGE,{"disambiguationData":[OSD([sQuery(id+"F85.wireOp",EDGE,"E42.bottom"),subQ0])]}),makeQuery(id+"F94.opExtrude","SWEPT_FACE",FACE,{"disambiguationData":[OSD([subQ0])]})],"blendedInto":[makeQuery(id+"F94.opExtrude","SWEPT_FACE",FACE,{"disambiguationData":[OSD([subQ0])]})]});}
            var Q4;
            {var subQ0=sQuery(id+"F82.wireOp",EDGE,"E39.top");Q4=makeQuery(id+"F99.opChamfer","BLEND_EDGE",EDGE,{"blendedFrom":[makeQuery(id+"F94.opExtrude","SWEPT_EDGE",EDGE,{"disambiguationData":[OSD([subQ0,sQuery(id+"F82.wireOp",EDGE,"E39.left")])]}),makeQuery(id+"F94.opExtrude","SWEPT_FACE",FACE,{"disambiguationData":[OSD([subQ0])]})],"blendedInto":[makeQuery(id+"F94.opExtrude","SWEPT_FACE",FACE,{"disambiguationData":[OSD([subQ0])]})]});}
            var Q5;
            {var subQ0=sQuery(id+"F82.wireOp",EDGE,"E39.top");Q5=makeQuery(id+"F99.opChamfer","BLEND_EDGE",EDGE,{"blendedFrom":[makeQuery(id+"F94.opExtrude","SWEPT_EDGE",EDGE,{"disambiguationData":[OSD([subQ0,sQuery(id+"F82.wireOp",EDGE,"E39.right")])]}),makeQuery(id+"F94.opExtrude","SWEPT_FACE",FACE,{"disambiguationData":[OSD([subQ0])]})],"blendedInto":[makeQuery(id+"F94.opExtrude","SWEPT_FACE",FACE,{"disambiguationData":[OSD([subQ0])]})]});}
            var Q6;
            {var subQ0=sQuery(id+"F83.wireOp",EDGE,"E40.right");Q6=makeQuery(id+"F100.opChamfer","BLEND_EDGE",EDGE,{"blendedFrom":[makeQuery(id+"F94.opExtrude","SWEPT_EDGE",EDGE,{"disambiguationData":[OSD([sQuery(id+"F83.wireOp",EDGE,"E40.bottom"),subQ0])]}),makeQuery(id+"F94.opExtrude","SWEPT_FACE",FACE,{"disambiguationData":[OSD([subQ0])]})],"blendedInto":[makeQuery(id+"F94.opExtrude","SWEPT_FACE",FACE,{"disambiguationData":[OSD([subQ0])]})]});}
            var Q7;
            {var subQ0=sQuery(id+"F83.wireOp",EDGE,"E40.right");Q7=makeQuery(id+"F99.opChamfer","BLEND_EDGE",EDGE,{"blendedFrom":[makeQuery(id+"F94.opExtrude","SWEPT_EDGE",EDGE,{"disambiguationData":[OSD([sQuery(id+"F83.wireOp",EDGE,"E40.top"),subQ0])]}),makeQuery(id+"F94.opExtrude","SWEPT_FACE",FACE,{"disambiguationData":[OSD([subQ0])]})],"blendedInto":[makeQuery(id+"F94.opExtrude","SWEPT_FACE",FACE,{"disambiguationData":[OSD([subQ0])]})]});}
            fillet(context, id + "F101", {"entities" : qUnion([Q0, Q1, Q2, Q3, Q4, Q5, Q6, Q7]), "radius" : 35.56 * mm, "tangentPropagation" : true, "allowEdgeOverflow" : false});
        }
        {
            var Q0;
            {var subQ0=sQuery(id+"F85.wireOp",EDGE,"E42.left");var subQ1=makeQuery(id+"F94.opExtrude","SWEPT_FACE",FACE,{"disambiguationData":[OSD([subQ0])]});Q0=makeQuery(id+"F101.opFillet","BLEND_EDGE",EDGE,{"blendedFrom":[makeQuery(id+"F99.opChamfer","BLEND_EDGE",EDGE,{"blendedFrom":[makeQuery(id+"F94.opExtrude","SWEPT_EDGE",EDGE,{"disambiguationData":[OSD([sQuery(id+"F85.wireOp",EDGE,"E42.bottom"),subQ0])]}),subQ1],"blendedInto":[subQ1]}),makeQuery(id+"F99.opChamfer","BLEND_EDGE",EDGE,{"blendedFrom":[makeQuery(id+"F94.opExtrude","SWEPT_EDGE",EDGE,{"disambiguationData":[OSD([sQuery(id+"F85.wireOp",EDGE,"E42.top"),subQ0])]}),subQ1],"blendedInto":[subQ1]})],"blendedInto":[]});}
            var Q1;
            {var subQ0=sQuery(id+"F82.wireOp",EDGE,"E39.top");var subQ1=makeQuery(id+"F94.opExtrude","SWEPT_FACE",FACE,{"disambiguationData":[OSD([subQ0])]});Q1=makeQuery(id+"F101.opFillet","BLEND_EDGE",EDGE,{"blendedFrom":[makeQuery(id+"F99.opChamfer","BLEND_EDGE",EDGE,{"blendedFrom":[makeQuery(id+"F94.opExtrude","SWEPT_EDGE",EDGE,{"disambiguationData":[OSD([subQ0,sQuery(id+"F82.wireOp",EDGE,"E39.left")])]}),subQ1],"blendedInto":[subQ1]}),makeQuery(id+"F99.opChamfer","BLEND_EDGE",EDGE,{"blendedFrom":[makeQuery(id+"F94.opExtrude","SWEPT_EDGE",EDGE,{"disambiguationData":[OSD([subQ0,sQuery(id+"F82.wireOp",EDGE,"E39.right")])]}),subQ1],"blendedInto":[subQ1]})],"blendedInto":[]});}
            var Q2;
            {var subQ0=sQuery(id+"F83.wireOp",EDGE,"E40.right");var subQ1=makeQuery(id+"F94.opExtrude","SWEPT_FACE",FACE,{"disambiguationData":[OSD([subQ0])]});Q2=makeQuery(id+"F101.opFillet","BLEND_EDGE",EDGE,{"blendedFrom":[makeQuery(id+"F99.opChamfer","BLEND_EDGE",EDGE,{"blendedFrom":[makeQuery(id+"F94.opExtrude","SWEPT_EDGE",EDGE,{"disambiguationData":[OSD([sQuery(id+"F83.wireOp",EDGE,"E40.top"),subQ0])]}),subQ1],"blendedInto":[subQ1]}),makeQuery(id+"F100.opChamfer","BLEND_EDGE",EDGE,{"blendedFrom":[makeQuery(id+"F94.opExtrude","SWEPT_EDGE",EDGE,{"disambiguationData":[OSD([sQuery(id+"F83.wireOp",EDGE,"E40.bottom"),subQ0])]}),subQ1],"blendedInto":[subQ1]})],"blendedInto":[]});}
            var Q3;
            {var subQ0=sQuery(id+"F86.wireOp",EDGE,"E43.bottom");var subQ1=makeQuery(id+"F94.opExtrude","SWEPT_FACE",FACE,{"disambiguationData":[OSD([subQ0])]});Q3=makeQuery(id+"F101.opFillet","BLEND_EDGE",EDGE,{"blendedFrom":[makeQuery(id+"F99.opChamfer","BLEND_EDGE",EDGE,{"blendedFrom":[makeQuery(id+"F94.opExtrude","SWEPT_EDGE",EDGE,{"disambiguationData":[OSD([subQ0,sQuery(id+"F86.wireOp",EDGE,"E43.left")])]}),subQ1],"blendedInto":[subQ1]}),makeQuery(id+"F99.opChamfer","BLEND_EDGE",EDGE,{"blendedFrom":[makeQuery(id+"F94.opExtrude","SWEPT_EDGE",EDGE,{"disambiguationData":[OSD([subQ0,sQuery(id+"F86.wireOp",EDGE,"E43.right")])]}),subQ1],"blendedInto":[subQ1]})],"blendedInto":[]});}
            fillet(context, id + "F102", {"entities" : qUnion([Q0, Q1, Q2, Q3]), "radius" : 25.4 * mm, "tangentPropagation" : true, "allowEdgeOverflow" : false});
        }
        {
            var Q0;
            {var subQ0=sQuery(id+"F75.wireOp",EDGE,"E33.bottom");Q0=makeQuery(id+"F99.opChamfer","BLEND_EDGE",EDGE,{"blendedFrom":[makeQuery(id+"F76.opExtrude","SWEPT_EDGE",EDGE,{"disambiguationData":[OSD([subQ0,sQuery(id+"F75.wireOp",EDGE,"E33.right")])]}),makeQuery(id+"F76.opExtrude","SWEPT_FACE",FACE,{"disambiguationData":[OSD([subQ0])]})],"blendedInto":[makeQuery(id+"F76.opExtrude","SWEPT_FACE",FACE,{"disambiguationData":[OSD([subQ0])]})]});}
            var Q1;
            {var subQ0=sQuery(id+"F75.wireOp",EDGE,"E33.bottom");Q1=makeQuery(id+"F99.opChamfer","BLEND_EDGE",EDGE,{"blendedFrom":[makeQuery(id+"F76.opExtrude","SWEPT_EDGE",EDGE,{"disambiguationData":[OSD([subQ0,sQuery(id+"F75.wireOp",EDGE,"E33.left")])]}),makeQuery(id+"F76.opExtrude","SWEPT_FACE",FACE,{"disambiguationData":[OSD([subQ0])]})],"blendedInto":[makeQuery(id+"F76.opExtrude","SWEPT_FACE",FACE,{"disambiguationData":[OSD([subQ0])]})]});}
            var Q2;
            {var subQ0=sQuery(id+"F74.wireOp",EDGE,"E32.left");Q2=makeQuery(id+"F99.opChamfer","BLEND_EDGE",EDGE,{"blendedFrom":[makeQuery(id+"F76.opExtrude","SWEPT_EDGE",EDGE,{"disambiguationData":[OSD([sQuery(id+"F74.wireOp",EDGE,"E32.top"),subQ0])]}),makeQuery(id+"F76.opExtrude","SWEPT_FACE",FACE,{"disambiguationData":[OSD([subQ0])]})],"blendedInto":[makeQuery(id+"F76.opExtrude","SWEPT_FACE",FACE,{"disambiguationData":[OSD([subQ0])]})]});}
            var Q3;
            {var subQ0=sQuery(id+"F74.wireOp",EDGE,"E32.left");Q3=makeQuery(id+"F99.opChamfer","BLEND_EDGE",EDGE,{"blendedFrom":[makeQuery(id+"F76.opExtrude","SWEPT_EDGE",EDGE,{"disambiguationData":[OSD([sQuery(id+"F74.wireOp",EDGE,"E32.bottom"),subQ0])]}),makeQuery(id+"F76.opExtrude","SWEPT_FACE",FACE,{"disambiguationData":[OSD([subQ0])]})],"blendedInto":[makeQuery(id+"F76.opExtrude","SWEPT_FACE",FACE,{"disambiguationData":[OSD([subQ0])]})]});}
            var Q4;
            {var subQ0=sQuery(id+"F72.wireOp",EDGE,"E30.right");Q4=makeQuery(id+"F99.opChamfer","BLEND_EDGE",EDGE,{"blendedFrom":[makeQuery(id+"F76.opExtrude","SWEPT_EDGE",EDGE,{"disambiguationData":[OSD([sQuery(id+"F72.wireOp",EDGE,"E30.bottom"),subQ0])]}),makeQuery(id+"F76.opExtrude","SWEPT_FACE",FACE,{"disambiguationData":[OSD([subQ0])]})],"blendedInto":[makeQuery(id+"F76.opExtrude","SWEPT_FACE",FACE,{"disambiguationData":[OSD([subQ0])]})]});}
            var Q5;
            {var subQ0=sQuery(id+"F72.wireOp",EDGE,"E30.right");Q5=makeQuery(id+"F99.opChamfer","BLEND_EDGE",EDGE,{"blendedFrom":[makeQuery(id+"F76.opExtrude","SWEPT_EDGE",EDGE,{"disambiguationData":[OSD([sQuery(id+"F72.wireOp",EDGE,"E30.top"),subQ0])]}),makeQuery(id+"F76.opExtrude","SWEPT_FACE",FACE,{"disambiguationData":[OSD([subQ0])]})],"blendedInto":[makeQuery(id+"F76.opExtrude","SWEPT_FACE",FACE,{"disambiguationData":[OSD([subQ0])]})]});}
            var Q6;
            {var subQ0=sQuery(id+"F69.wireOp",EDGE,"E28.left");Q6=makeQuery(id+"F99.opChamfer","BLEND_EDGE",EDGE,{"blendedFrom":[makeQuery(id+"F70.opExtrude","SWEPT_EDGE",EDGE,{"disambiguationData":[OSD([sQuery(id+"F69.wireOp",EDGE,"E28.top"),subQ0])]}),makeQuery(id+"F70.opExtrude","SWEPT_FACE",FACE,{"disambiguationData":[OSD([subQ0])]})],"blendedInto":[makeQuery(id+"F70.opExtrude","SWEPT_FACE",FACE,{"disambiguationData":[OSD([subQ0])]})]});}
            var Q7;
            {var subQ0=sQuery(id+"F69.wireOp",EDGE,"E28.left");Q7=makeQuery(id+"F99.opChamfer","BLEND_EDGE",EDGE,{"blendedFrom":[makeQuery(id+"F70.opExtrude","SWEPT_EDGE",EDGE,{"disambiguationData":[OSD([sQuery(id+"F69.wireOp",EDGE,"E28.bottom"),subQ0])]}),makeQuery(id+"F70.opExtrude","SWEPT_FACE",FACE,{"disambiguationData":[OSD([subQ0])]})],"blendedInto":[makeQuery(id+"F70.opExtrude","SWEPT_FACE",FACE,{"disambiguationData":[OSD([subQ0])]})]});}
            var Q8;
            {var subQ0=sQuery(id+"F68.wireOp",EDGE,"E27.bottom");Q8=makeQuery(id+"F99.opChamfer","BLEND_EDGE",EDGE,{"blendedFrom":[makeQuery(id+"F70.opExtrude","SWEPT_EDGE",EDGE,{"disambiguationData":[OSD([subQ0,sQuery(id+"F68.wireOp",EDGE,"E27.right")])]}),makeQuery(id+"F70.opExtrude","SWEPT_FACE",FACE,{"disambiguationData":[OSD([subQ0])]})],"blendedInto":[makeQuery(id+"F70.opExtrude","SWEPT_FACE",FACE,{"disambiguationData":[OSD([subQ0])]})]});}
            var Q9;
            {var subQ0=sQuery(id+"F68.wireOp",EDGE,"E27.bottom");Q9=makeQuery(id+"F99.opChamfer","BLEND_EDGE",EDGE,{"blendedFrom":[makeQuery(id+"F70.opExtrude","SWEPT_EDGE",EDGE,{"disambiguationData":[OSD([subQ0,sQuery(id+"F68.wireOp",EDGE,"E27.left")])]}),makeQuery(id+"F70.opExtrude","SWEPT_FACE",FACE,{"disambiguationData":[OSD([subQ0])]})],"blendedInto":[makeQuery(id+"F70.opExtrude","SWEPT_FACE",FACE,{"disambiguationData":[OSD([subQ0])]})]});}
            var Q10;
            {var subQ0=sQuery(id+"F66.wireOp",EDGE,"E25.top");Q10=makeQuery(id+"F99.opChamfer","BLEND_EDGE",EDGE,{"blendedFrom":[makeQuery(id+"F70.opExtrude","SWEPT_EDGE",EDGE,{"disambiguationData":[OSD([subQ0,sQuery(id+"F66.wireOp",EDGE,"E25.right")])]}),makeQuery(id+"F70.opExtrude","SWEPT_FACE",FACE,{"disambiguationData":[OSD([subQ0])]})],"blendedInto":[makeQuery(id+"F70.opExtrude","SWEPT_FACE",FACE,{"disambiguationData":[OSD([subQ0])]})]});}
            var Q11;
            {var subQ0=sQuery(id+"F66.wireOp",EDGE,"E25.top");Q11=makeQuery(id+"F99.opChamfer","BLEND_EDGE",EDGE,{"blendedFrom":[makeQuery(id+"F70.opExtrude","SWEPT_EDGE",EDGE,{"disambiguationData":[OSD([subQ0,sQuery(id+"F66.wireOp",EDGE,"E25.left")])]}),makeQuery(id+"F70.opExtrude","SWEPT_FACE",FACE,{"disambiguationData":[OSD([subQ0])]})],"blendedInto":[makeQuery(id+"F70.opExtrude","SWEPT_FACE",FACE,{"disambiguationData":[OSD([subQ0])]})]});}
            var Q12;
            {var subQ0=sQuery(id+"F65.wireOp",EDGE,"E24.right");Q12=makeQuery(id+"F99.opChamfer","BLEND_EDGE",EDGE,{"blendedFrom":[makeQuery(id+"F70.opExtrude","SWEPT_EDGE",EDGE,{"disambiguationData":[OSD([sQuery(id+"F65.wireOp",EDGE,"E24.top"),subQ0])]}),makeQuery(id+"F70.opExtrude","SWEPT_FACE",FACE,{"disambiguationData":[OSD([subQ0])]})],"blendedInto":[makeQuery(id+"F70.opExtrude","SWEPT_FACE",FACE,{"disambiguationData":[OSD([subQ0])]})]});}
            var Q13;
            {var subQ0=sQuery(id+"F65.wireOp",EDGE,"E24.right");Q13=makeQuery(id+"F99.opChamfer","BLEND_EDGE",EDGE,{"blendedFrom":[makeQuery(id+"F70.opExtrude","SWEPT_EDGE",EDGE,{"disambiguationData":[OSD([sQuery(id+"F65.wireOp",EDGE,"E24.bottom"),subQ0])]}),makeQuery(id+"F70.opExtrude","SWEPT_FACE",FACE,{"disambiguationData":[OSD([subQ0])]})],"blendedInto":[makeQuery(id+"F70.opExtrude","SWEPT_FACE",FACE,{"disambiguationData":[OSD([subQ0])]})]});}
            var Q14;
            {var subQ0=sQuery(id+"F54.wireOp",EDGE,"E17.right");Q14=makeQuery(id+"F99.opChamfer","BLEND_EDGE",EDGE,{"blendedFrom":[makeQuery(id+"F64.opExtrude","SWEPT_EDGE",EDGE,{"disambiguationData":[OSD([sQuery(id+"F54.wireOp",EDGE,"E17.top"),subQ0])]}),makeQuery(id+"F64.opExtrude","SWEPT_FACE",FACE,{"disambiguationData":[OSD([subQ0])]})],"blendedInto":[makeQuery(id+"F64.opExtrude","SWEPT_FACE",FACE,{"disambiguationData":[OSD([subQ0])]})]});}
            var Q15;
            {var subQ0=sQuery(id+"F58.wireOp",EDGE,"E21.bottom");Q15=makeQuery(id+"F99.opChamfer","BLEND_EDGE",EDGE,{"blendedFrom":[makeQuery(id+"F64.opExtrude","SWEPT_EDGE",EDGE,{"disambiguationData":[OSD([subQ0,sQuery(id+"F58.wireOp",EDGE,"E21.left")])]}),makeQuery(id+"F64.opExtrude","SWEPT_FACE",FACE,{"disambiguationData":[OSD([subQ0])]})],"blendedInto":[makeQuery(id+"F64.opExtrude","SWEPT_FACE",FACE,{"disambiguationData":[OSD([subQ0])]})]});}
            var Q16;
            {var subQ0=sQuery(id+"F54.wireOp",EDGE,"E17.right");Q16=makeQuery(id+"F99.opChamfer","BLEND_EDGE",EDGE,{"blendedFrom":[makeQuery(id+"F64.opExtrude","SWEPT_EDGE",EDGE,{"disambiguationData":[OSD([sQuery(id+"F54.wireOp",EDGE,"E17.bottom"),subQ0])]}),makeQuery(id+"F64.opExtrude","SWEPT_FACE",FACE,{"disambiguationData":[OSD([subQ0])]})],"blendedInto":[makeQuery(id+"F64.opExtrude","SWEPT_FACE",FACE,{"disambiguationData":[OSD([subQ0])]})]});}
            var Q17;
            {var subQ0=sQuery(id+"F58.wireOp",EDGE,"E21.bottom");Q17=makeQuery(id+"F99.opChamfer","BLEND_EDGE",EDGE,{"blendedFrom":[makeQuery(id+"F64.opExtrude","SWEPT_EDGE",EDGE,{"disambiguationData":[OSD([subQ0,sQuery(id+"F58.wireOp",EDGE,"E21.right")])]}),makeQuery(id+"F64.opExtrude","SWEPT_FACE",FACE,{"disambiguationData":[OSD([subQ0])]})],"blendedInto":[makeQuery(id+"F64.opExtrude","SWEPT_FACE",FACE,{"disambiguationData":[OSD([subQ0])]})]});}
            var Q18;
            {var subQ0=sQuery(id+"F60.wireOp",EDGE,"E23.left");Q18=makeQuery(id+"F99.opChamfer","BLEND_EDGE",EDGE,{"blendedFrom":[makeQuery(id+"F64.opExtrude","SWEPT_EDGE",EDGE,{"disambiguationData":[OSD([sQuery(id+"F60.wireOp",EDGE,"E23.bottom"),subQ0])]}),makeQuery(id+"F64.opExtrude","SWEPT_FACE",FACE,{"disambiguationData":[OSD([subQ0])]})],"blendedInto":[makeQuery(id+"F64.opExtrude","SWEPT_FACE",FACE,{"disambiguationData":[OSD([subQ0])]})]});}
            var Q19;
            {var subQ0=sQuery(id+"F60.wireOp",EDGE,"E23.left");Q19=makeQuery(id+"F99.opChamfer","BLEND_EDGE",EDGE,{"blendedFrom":[makeQuery(id+"F64.opExtrude","SWEPT_EDGE",EDGE,{"disambiguationData":[OSD([sQuery(id+"F60.wireOp",EDGE,"E23.top"),subQ0])]}),makeQuery(id+"F64.opExtrude","SWEPT_FACE",FACE,{"disambiguationData":[OSD([subQ0])]})],"blendedInto":[makeQuery(id+"F64.opExtrude","SWEPT_FACE",FACE,{"disambiguationData":[OSD([subQ0])]})]});}
            var Q20;
            {var subQ0=sQuery(id+"F56.wireOp",EDGE,"E19.top");Q20=makeQuery(id+"F99.opChamfer","BLEND_EDGE",EDGE,{"blendedFrom":[makeQuery(id+"F64.opExtrude","SWEPT_EDGE",EDGE,{"disambiguationData":[OSD([subQ0,sQuery(id+"F56.wireOp",EDGE,"E19.left")])]}),makeQuery(id+"F64.opExtrude","SWEPT_FACE",FACE,{"disambiguationData":[OSD([subQ0])]})],"blendedInto":[makeQuery(id+"F64.opExtrude","SWEPT_FACE",FACE,{"disambiguationData":[OSD([subQ0])]})]});}
            var Q21;
            {var subQ0=sQuery(id+"F56.wireOp",EDGE,"E19.top");Q21=makeQuery(id+"F99.opChamfer","BLEND_EDGE",EDGE,{"blendedFrom":[makeQuery(id+"F64.opExtrude","SWEPT_EDGE",EDGE,{"disambiguationData":[OSD([subQ0,sQuery(id+"F56.wireOp",EDGE,"E19.right")])]}),makeQuery(id+"F64.opExtrude","SWEPT_FACE",FACE,{"disambiguationData":[OSD([subQ0])]})],"blendedInto":[makeQuery(id+"F64.opExtrude","SWEPT_FACE",FACE,{"disambiguationData":[OSD([subQ0])]})]});}
            var Q22;
            {var subQ0=sQuery(id+"F80.wireOp",EDGE,"E37.left");Q22=makeQuery(id+"F99.opChamfer","BLEND_EDGE",EDGE,{"blendedFrom":[makeQuery(id+"F93.opExtrude","SWEPT_EDGE",EDGE,{"disambiguationData":[OSD([sQuery(id+"F80.wireOp",EDGE,"E37.top"),subQ0])]}),makeQuery(id+"F93.opExtrude","SWEPT_FACE",FACE,{"disambiguationData":[OSD([subQ0])]})],"blendedInto":[makeQuery(id+"F93.opExtrude","SWEPT_FACE",FACE,{"disambiguationData":[OSD([subQ0])]})]});}
            var Q23;
            {var subQ0=sQuery(id+"F80.wireOp",EDGE,"E37.left");Q23=makeQuery(id+"F99.opChamfer","BLEND_EDGE",EDGE,{"blendedFrom":[makeQuery(id+"F93.opExtrude","SWEPT_EDGE",EDGE,{"disambiguationData":[OSD([sQuery(id+"F80.wireOp",EDGE,"E37.bottom"),subQ0])]}),makeQuery(id+"F93.opExtrude","SWEPT_FACE",FACE,{"disambiguationData":[OSD([subQ0])]})],"blendedInto":[makeQuery(id+"F93.opExtrude","SWEPT_FACE",FACE,{"disambiguationData":[OSD([subQ0])]})]});}
            var Q24;
            {var subQ0=sQuery(id+"F81.wireOp",EDGE,"E38.bottom");Q24=makeQuery(id+"F99.opChamfer","BLEND_EDGE",EDGE,{"blendedFrom":[makeQuery(id+"F93.opExtrude","SWEPT_EDGE",EDGE,{"disambiguationData":[OSD([subQ0,sQuery(id+"F81.wireOp",EDGE,"E38.right")])]}),makeQuery(id+"F93.opExtrude","SWEPT_FACE",FACE,{"disambiguationData":[OSD([subQ0])]})],"blendedInto":[makeQuery(id+"F93.opExtrude","SWEPT_FACE",FACE,{"disambiguationData":[OSD([subQ0])]})]});}
            var Q25;
            {var subQ0=sQuery(id+"F81.wireOp",EDGE,"E38.bottom");Q25=makeQuery(id+"F99.opChamfer","BLEND_EDGE",EDGE,{"blendedFrom":[makeQuery(id+"F93.opExtrude","SWEPT_EDGE",EDGE,{"disambiguationData":[OSD([subQ0,sQuery(id+"F81.wireOp",EDGE,"E38.left")])]}),makeQuery(id+"F93.opExtrude","SWEPT_FACE",FACE,{"disambiguationData":[OSD([subQ0])]})],"blendedInto":[makeQuery(id+"F93.opExtrude","SWEPT_FACE",FACE,{"disambiguationData":[OSD([subQ0])]})]});}
            var Q26;
            {var subQ0=sQuery(id+"F78.wireOp",EDGE,"E35.right");Q26=makeQuery(id+"F99.opChamfer","BLEND_EDGE",EDGE,{"blendedFrom":[makeQuery(id+"F93.opExtrude","SWEPT_EDGE",EDGE,{"disambiguationData":[OSD([sQuery(id+"F78.wireOp",EDGE,"E35.bottom"),subQ0])]}),makeQuery(id+"F93.opExtrude","SWEPT_FACE",FACE,{"disambiguationData":[OSD([subQ0])]})],"blendedInto":[makeQuery(id+"F93.opExtrude","SWEPT_FACE",FACE,{"disambiguationData":[OSD([subQ0])]})]});}
            var Q27;
            {var subQ0=sQuery(id+"F78.wireOp",EDGE,"E35.right");Q27=makeQuery(id+"F99.opChamfer","BLEND_EDGE",EDGE,{"blendedFrom":[makeQuery(id+"F93.opExtrude","SWEPT_EDGE",EDGE,{"disambiguationData":[OSD([sQuery(id+"F78.wireOp",EDGE,"E35.top"),subQ0])]}),makeQuery(id+"F93.opExtrude","SWEPT_FACE",FACE,{"disambiguationData":[OSD([subQ0])]})],"blendedInto":[makeQuery(id+"F93.opExtrude","SWEPT_FACE",FACE,{"disambiguationData":[OSD([subQ0])]})]});}
            var Q28;
            {var subQ0=sQuery(id+"F77.wireOp",EDGE,"E34.top");Q28=makeQuery(id+"F99.opChamfer","BLEND_EDGE",EDGE,{"blendedFrom":[makeQuery(id+"F93.opExtrude","SWEPT_EDGE",EDGE,{"disambiguationData":[OSD([subQ0,sQuery(id+"F77.wireOp",EDGE,"E34.left")])]}),makeQuery(id+"F93.opExtrude","SWEPT_FACE",FACE,{"disambiguationData":[OSD([subQ0])]})],"blendedInto":[makeQuery(id+"F93.opExtrude","SWEPT_FACE",FACE,{"disambiguationData":[OSD([subQ0])]})]});}
            var Q29;
            {var subQ0=sQuery(id+"F77.wireOp",EDGE,"E34.top");Q29=makeQuery(id+"F99.opChamfer","BLEND_EDGE",EDGE,{"blendedFrom":[makeQuery(id+"F93.opExtrude","SWEPT_EDGE",EDGE,{"disambiguationData":[OSD([subQ0,sQuery(id+"F77.wireOp",EDGE,"E34.right")])]}),makeQuery(id+"F93.opExtrude","SWEPT_FACE",FACE,{"disambiguationData":[OSD([subQ0])]})],"blendedInto":[makeQuery(id+"F93.opExtrude","SWEPT_FACE",FACE,{"disambiguationData":[OSD([subQ0])]})]});}
            var Q30;
            {var subQ0=sQuery(id+"F91.wireOp",EDGE,"E48.bottom");Q30=makeQuery(id+"F99.opChamfer","BLEND_EDGE",EDGE,{"blendedFrom":[makeQuery(id+"F92.opExtrude","SWEPT_EDGE",EDGE,{"disambiguationData":[OSD([subQ0,sQuery(id+"F91.wireOp",EDGE,"E48.left")])]}),makeQuery(id+"F92.opExtrude","SWEPT_FACE",FACE,{"disambiguationData":[OSD([subQ0])]})],"blendedInto":[makeQuery(id+"F92.opExtrude","SWEPT_FACE",FACE,{"disambiguationData":[OSD([subQ0])]})]});}
            var Q31;
            {var subQ0=sQuery(id+"F88.wireOp",EDGE,"E45.right");Q31=makeQuery(id+"F99.opChamfer","BLEND_EDGE",EDGE,{"blendedFrom":[makeQuery(id+"F92.opExtrude","SWEPT_EDGE",EDGE,{"disambiguationData":[OSD([sQuery(id+"F88.wireOp",EDGE,"E45.top"),subQ0])]}),makeQuery(id+"F92.opExtrude","SWEPT_FACE",FACE,{"disambiguationData":[OSD([subQ0])]})],"blendedInto":[makeQuery(id+"F92.opExtrude","SWEPT_FACE",FACE,{"disambiguationData":[OSD([subQ0])]})]});}
            var Q32;
            {var subQ0=sQuery(id+"F88.wireOp",EDGE,"E45.right");Q32=makeQuery(id+"F99.opChamfer","BLEND_EDGE",EDGE,{"blendedFrom":[makeQuery(id+"F92.opExtrude","SWEPT_EDGE",EDGE,{"disambiguationData":[OSD([sQuery(id+"F88.wireOp",EDGE,"E45.bottom"),subQ0])]}),makeQuery(id+"F92.opExtrude","SWEPT_FACE",FACE,{"disambiguationData":[OSD([subQ0])]})],"blendedInto":[makeQuery(id+"F92.opExtrude","SWEPT_FACE",FACE,{"disambiguationData":[OSD([subQ0])]})]});}
            var Q33;
            {var subQ0=sQuery(id+"F91.wireOp",EDGE,"E48.bottom");Q33=makeQuery(id+"F99.opChamfer","BLEND_EDGE",EDGE,{"blendedFrom":[makeQuery(id+"F92.opExtrude","SWEPT_EDGE",EDGE,{"disambiguationData":[OSD([subQ0,sQuery(id+"F91.wireOp",EDGE,"E48.right")])]}),makeQuery(id+"F92.opExtrude","SWEPT_FACE",FACE,{"disambiguationData":[OSD([subQ0])]})],"blendedInto":[makeQuery(id+"F92.opExtrude","SWEPT_FACE",FACE,{"disambiguationData":[OSD([subQ0])]})]});}
            var Q34;
            {var subQ0=sQuery(id+"F87.wireOp",EDGE,"E44.top");Q34=makeQuery(id+"F99.opChamfer","BLEND_EDGE",EDGE,{"blendedFrom":[makeQuery(id+"F92.opExtrude","SWEPT_EDGE",EDGE,{"disambiguationData":[OSD([subQ0,sQuery(id+"F87.wireOp",EDGE,"E44.right")])]}),makeQuery(id+"F92.opExtrude","SWEPT_FACE",FACE,{"disambiguationData":[OSD([subQ0])]})],"blendedInto":[makeQuery(id+"F92.opExtrude","SWEPT_FACE",FACE,{"disambiguationData":[OSD([subQ0])]})]});}
            var Q35;
            {var subQ0=sQuery(id+"F87.wireOp",EDGE,"E44.top");Q35=makeQuery(id+"F99.opChamfer","BLEND_EDGE",EDGE,{"blendedFrom":[makeQuery(id+"F92.opExtrude","SWEPT_EDGE",EDGE,{"disambiguationData":[OSD([subQ0,sQuery(id+"F87.wireOp",EDGE,"E44.left")])]}),makeQuery(id+"F92.opExtrude","SWEPT_FACE",FACE,{"disambiguationData":[OSD([subQ0])]})],"blendedInto":[makeQuery(id+"F92.opExtrude","SWEPT_FACE",FACE,{"disambiguationData":[OSD([subQ0])]})]});}
            var Q36;
            {var subQ0=sQuery(id+"F90.wireOp",EDGE,"E47.left");Q36=makeQuery(id+"F99.opChamfer","BLEND_EDGE",EDGE,{"blendedFrom":[makeQuery(id+"F92.opExtrude","SWEPT_EDGE",EDGE,{"disambiguationData":[OSD([sQuery(id+"F90.wireOp",EDGE,"E47.bottom"),subQ0])]}),makeQuery(id+"F92.opExtrude","SWEPT_FACE",FACE,{"disambiguationData":[OSD([subQ0])]})],"blendedInto":[makeQuery(id+"F92.opExtrude","SWEPT_FACE",FACE,{"disambiguationData":[OSD([subQ0])]})]});}
            var Q37;
            {var subQ0=sQuery(id+"F90.wireOp",EDGE,"E47.left");Q37=makeQuery(id+"F99.opChamfer","BLEND_EDGE",EDGE,{"blendedFrom":[makeQuery(id+"F92.opExtrude","SWEPT_EDGE",EDGE,{"disambiguationData":[OSD([sQuery(id+"F90.wireOp",EDGE,"E47.top"),subQ0])]}),makeQuery(id+"F92.opExtrude","SWEPT_FACE",FACE,{"disambiguationData":[OSD([subQ0])]})],"blendedInto":[makeQuery(id+"F92.opExtrude","SWEPT_FACE",FACE,{"disambiguationData":[OSD([subQ0])]})]});}
            fillet(context, id + "F103", {"entities" : qUnion([Q0, Q1, Q2, Q3, Q4, Q5, Q6, Q7, Q8, Q9, Q10, Q11, Q12, Q13, Q14, Q15, Q16, Q17, Q18, Q19, Q20, Q21, Q22, Q23, Q24, Q25, Q26, Q27, Q28, Q29, Q30, Q31, Q32, Q33, Q34, Q35, Q36, Q37]), "radius" : 35.56 * mm, "tangentPropagation" : true, "allowEdgeOverflow" : false});
        }
        {
            var Q0;
            {var subQ0=sQuery(id+"F72.wireOp",EDGE,"E30.right");var subQ1=makeQuery(id+"F76.opExtrude","SWEPT_FACE",FACE,{"disambiguationData":[OSD([subQ0])]});Q0=makeQuery(id+"F103.opFillet","BLEND_EDGE",EDGE,{"blendedFrom":[makeQuery(id+"F99.opChamfer","BLEND_EDGE",EDGE,{"blendedFrom":[makeQuery(id+"F76.opExtrude","SWEPT_EDGE",EDGE,{"disambiguationData":[OSD([sQuery(id+"F72.wireOp",EDGE,"E30.bottom"),subQ0])]}),subQ1],"blendedInto":[subQ1]}),makeQuery(id+"F99.opChamfer","BLEND_EDGE",EDGE,{"blendedFrom":[makeQuery(id+"F76.opExtrude","SWEPT_EDGE",EDGE,{"disambiguationData":[OSD([sQuery(id+"F72.wireOp",EDGE,"E30.top"),subQ0])]}),subQ1],"blendedInto":[subQ1]})],"blendedInto":[]});}
            var Q1;
            {var subQ0=sQuery(id+"F75.wireOp",EDGE,"E33.bottom");var subQ1=makeQuery(id+"F76.opExtrude","SWEPT_FACE",FACE,{"disambiguationData":[OSD([subQ0])]});Q1=makeQuery(id+"F103.opFillet","BLEND_EDGE",EDGE,{"blendedFrom":[makeQuery(id+"F99.opChamfer","BLEND_EDGE",EDGE,{"blendedFrom":[makeQuery(id+"F76.opExtrude","SWEPT_EDGE",EDGE,{"disambiguationData":[OSD([subQ0,sQuery(id+"F75.wireOp",EDGE,"E33.left")])]}),subQ1],"blendedInto":[subQ1]}),makeQuery(id+"F99.opChamfer","BLEND_EDGE",EDGE,{"blendedFrom":[makeQuery(id+"F76.opExtrude","SWEPT_EDGE",EDGE,{"disambiguationData":[OSD([subQ0,sQuery(id+"F75.wireOp",EDGE,"E33.right")])]}),subQ1],"blendedInto":[subQ1]})],"blendedInto":[]});}
            var Q2;
            {var subQ0=sQuery(id+"F74.wireOp",EDGE,"E32.left");var subQ1=makeQuery(id+"F76.opExtrude","SWEPT_FACE",FACE,{"disambiguationData":[OSD([subQ0])]});Q2=makeQuery(id+"F103.opFillet","BLEND_EDGE",EDGE,{"blendedFrom":[makeQuery(id+"F99.opChamfer","BLEND_EDGE",EDGE,{"blendedFrom":[makeQuery(id+"F76.opExtrude","SWEPT_EDGE",EDGE,{"disambiguationData":[OSD([sQuery(id+"F74.wireOp",EDGE,"E32.bottom"),subQ0])]}),subQ1],"blendedInto":[subQ1]}),makeQuery(id+"F99.opChamfer","BLEND_EDGE",EDGE,{"blendedFrom":[makeQuery(id+"F76.opExtrude","SWEPT_EDGE",EDGE,{"disambiguationData":[OSD([sQuery(id+"F74.wireOp",EDGE,"E32.top"),subQ0])]}),subQ1],"blendedInto":[subQ1]})],"blendedInto":[]});}
            var Q3;
            {var subQ0=sQuery(id+"F87.wireOp",EDGE,"E44.top");var subQ1=makeQuery(id+"F92.opExtrude","SWEPT_FACE",FACE,{"disambiguationData":[OSD([subQ0])]});Q3=makeQuery(id+"F103.opFillet","BLEND_EDGE",EDGE,{"blendedFrom":[makeQuery(id+"F99.opChamfer","BLEND_EDGE",EDGE,{"blendedFrom":[makeQuery(id+"F92.opExtrude","SWEPT_EDGE",EDGE,{"disambiguationData":[OSD([subQ0,sQuery(id+"F87.wireOp",EDGE,"E44.left")])]}),subQ1],"blendedInto":[subQ1]}),makeQuery(id+"F99.opChamfer","BLEND_EDGE",EDGE,{"blendedFrom":[makeQuery(id+"F92.opExtrude","SWEPT_EDGE",EDGE,{"disambiguationData":[OSD([subQ0,sQuery(id+"F87.wireOp",EDGE,"E44.right")])]}),subQ1],"blendedInto":[subQ1]})],"blendedInto":[]});}
            var Q4;
            {var subQ0=sQuery(id+"F88.wireOp",EDGE,"E45.right");var subQ1=makeQuery(id+"F92.opExtrude","SWEPT_FACE",FACE,{"disambiguationData":[OSD([subQ0])]});Q4=makeQuery(id+"F103.opFillet","BLEND_EDGE",EDGE,{"blendedFrom":[makeQuery(id+"F99.opChamfer","BLEND_EDGE",EDGE,{"blendedFrom":[makeQuery(id+"F92.opExtrude","SWEPT_EDGE",EDGE,{"disambiguationData":[OSD([sQuery(id+"F88.wireOp",EDGE,"E45.bottom"),subQ0])]}),subQ1],"blendedInto":[subQ1]}),makeQuery(id+"F99.opChamfer","BLEND_EDGE",EDGE,{"blendedFrom":[makeQuery(id+"F92.opExtrude","SWEPT_EDGE",EDGE,{"disambiguationData":[OSD([sQuery(id+"F88.wireOp",EDGE,"E45.top"),subQ0])]}),subQ1],"blendedInto":[subQ1]})],"blendedInto":[]});}
            var Q5;
            {var subQ0=sQuery(id+"F90.wireOp",EDGE,"E47.left");var subQ1=makeQuery(id+"F92.opExtrude","SWEPT_FACE",FACE,{"disambiguationData":[OSD([subQ0])]});Q5=makeQuery(id+"F103.opFillet","BLEND_EDGE",EDGE,{"blendedFrom":[makeQuery(id+"F99.opChamfer","BLEND_EDGE",EDGE,{"blendedFrom":[makeQuery(id+"F92.opExtrude","SWEPT_EDGE",EDGE,{"disambiguationData":[OSD([sQuery(id+"F90.wireOp",EDGE,"E47.bottom"),subQ0])]}),subQ1],"blendedInto":[subQ1]}),makeQuery(id+"F99.opChamfer","BLEND_EDGE",EDGE,{"blendedFrom":[makeQuery(id+"F92.opExtrude","SWEPT_EDGE",EDGE,{"disambiguationData":[OSD([sQuery(id+"F90.wireOp",EDGE,"E47.top"),subQ0])]}),subQ1],"blendedInto":[subQ1]})],"blendedInto":[]});}
            var Q6;
            {var subQ0=sQuery(id+"F91.wireOp",EDGE,"E48.bottom");var subQ1=makeQuery(id+"F92.opExtrude","SWEPT_FACE",FACE,{"disambiguationData":[OSD([subQ0])]});Q6=makeQuery(id+"F103.opFillet","BLEND_EDGE",EDGE,{"blendedFrom":[makeQuery(id+"F99.opChamfer","BLEND_EDGE",EDGE,{"blendedFrom":[makeQuery(id+"F92.opExtrude","SWEPT_EDGE",EDGE,{"disambiguationData":[OSD([subQ0,sQuery(id+"F91.wireOp",EDGE,"E48.left")])]}),subQ1],"blendedInto":[subQ1]}),makeQuery(id+"F99.opChamfer","BLEND_EDGE",EDGE,{"blendedFrom":[makeQuery(id+"F92.opExtrude","SWEPT_EDGE",EDGE,{"disambiguationData":[OSD([subQ0,sQuery(id+"F91.wireOp",EDGE,"E48.right")])]}),subQ1],"blendedInto":[subQ1]})],"blendedInto":[]});}
            var Q7;
            {var subQ0=sQuery(id+"F80.wireOp",EDGE,"E37.left");var subQ1=makeQuery(id+"F93.opExtrude","SWEPT_FACE",FACE,{"disambiguationData":[OSD([subQ0])]});Q7=makeQuery(id+"F103.opFillet","BLEND_EDGE",EDGE,{"blendedFrom":[makeQuery(id+"F99.opChamfer","BLEND_EDGE",EDGE,{"blendedFrom":[makeQuery(id+"F93.opExtrude","SWEPT_EDGE",EDGE,{"disambiguationData":[OSD([sQuery(id+"F80.wireOp",EDGE,"E37.bottom"),subQ0])]}),subQ1],"blendedInto":[subQ1]}),makeQuery(id+"F99.opChamfer","BLEND_EDGE",EDGE,{"blendedFrom":[makeQuery(id+"F93.opExtrude","SWEPT_EDGE",EDGE,{"disambiguationData":[OSD([sQuery(id+"F80.wireOp",EDGE,"E37.top"),subQ0])]}),subQ1],"blendedInto":[subQ1]})],"blendedInto":[]});}
            var Q8;
            {var subQ0=sQuery(id+"F77.wireOp",EDGE,"E34.top");var subQ1=makeQuery(id+"F93.opExtrude","SWEPT_FACE",FACE,{"disambiguationData":[OSD([subQ0])]});Q8=makeQuery(id+"F103.opFillet","BLEND_EDGE",EDGE,{"blendedFrom":[makeQuery(id+"F99.opChamfer","BLEND_EDGE",EDGE,{"blendedFrom":[makeQuery(id+"F93.opExtrude","SWEPT_EDGE",EDGE,{"disambiguationData":[OSD([subQ0,sQuery(id+"F77.wireOp",EDGE,"E34.left")])]}),subQ1],"blendedInto":[subQ1]}),makeQuery(id+"F99.opChamfer","BLEND_EDGE",EDGE,{"blendedFrom":[makeQuery(id+"F93.opExtrude","SWEPT_EDGE",EDGE,{"disambiguationData":[OSD([subQ0,sQuery(id+"F77.wireOp",EDGE,"E34.right")])]}),subQ1],"blendedInto":[subQ1]})],"blendedInto":[]});}
            var Q9;
            {var subQ0=sQuery(id+"F78.wireOp",EDGE,"E35.right");var subQ1=makeQuery(id+"F93.opExtrude","SWEPT_FACE",FACE,{"disambiguationData":[OSD([subQ0])]});Q9=makeQuery(id+"F103.opFillet","BLEND_EDGE",EDGE,{"blendedFrom":[makeQuery(id+"F99.opChamfer","BLEND_EDGE",EDGE,{"blendedFrom":[makeQuery(id+"F93.opExtrude","SWEPT_EDGE",EDGE,{"disambiguationData":[OSD([sQuery(id+"F78.wireOp",EDGE,"E35.bottom"),subQ0])]}),subQ1],"blendedInto":[subQ1]}),makeQuery(id+"F99.opChamfer","BLEND_EDGE",EDGE,{"blendedFrom":[makeQuery(id+"F93.opExtrude","SWEPT_EDGE",EDGE,{"disambiguationData":[OSD([sQuery(id+"F78.wireOp",EDGE,"E35.top"),subQ0])]}),subQ1],"blendedInto":[subQ1]})],"blendedInto":[]});}
            var Q10;
            {var subQ0=sQuery(id+"F81.wireOp",EDGE,"E38.bottom");var subQ1=makeQuery(id+"F93.opExtrude","SWEPT_FACE",FACE,{"disambiguationData":[OSD([subQ0])]});Q10=makeQuery(id+"F103.opFillet","BLEND_EDGE",EDGE,{"blendedFrom":[makeQuery(id+"F99.opChamfer","BLEND_EDGE",EDGE,{"blendedFrom":[makeQuery(id+"F93.opExtrude","SWEPT_EDGE",EDGE,{"disambiguationData":[OSD([subQ0,sQuery(id+"F81.wireOp",EDGE,"E38.left")])]}),subQ1],"blendedInto":[subQ1]}),makeQuery(id+"F99.opChamfer","BLEND_EDGE",EDGE,{"blendedFrom":[makeQuery(id+"F93.opExtrude","SWEPT_EDGE",EDGE,{"disambiguationData":[OSD([subQ0,sQuery(id+"F81.wireOp",EDGE,"E38.right")])]}),subQ1],"blendedInto":[subQ1]})],"blendedInto":[]});}
            var Q11;
            {var subQ0=sQuery(id+"F60.wireOp",EDGE,"E23.left");var subQ1=makeQuery(id+"F64.opExtrude","SWEPT_FACE",FACE,{"disambiguationData":[OSD([subQ0])]});Q11=makeQuery(id+"F103.opFillet","BLEND_EDGE",EDGE,{"blendedFrom":[makeQuery(id+"F99.opChamfer","BLEND_EDGE",EDGE,{"blendedFrom":[makeQuery(id+"F64.opExtrude","SWEPT_EDGE",EDGE,{"disambiguationData":[OSD([sQuery(id+"F60.wireOp",EDGE,"E23.bottom"),subQ0])]}),subQ1],"blendedInto":[subQ1]}),makeQuery(id+"F99.opChamfer","BLEND_EDGE",EDGE,{"blendedFrom":[makeQuery(id+"F64.opExtrude","SWEPT_EDGE",EDGE,{"disambiguationData":[OSD([sQuery(id+"F60.wireOp",EDGE,"E23.top"),subQ0])]}),subQ1],"blendedInto":[subQ1]})],"blendedInto":[]});}
            var Q12;
            {var subQ0=sQuery(id+"F58.wireOp",EDGE,"E21.bottom");var subQ1=makeQuery(id+"F64.opExtrude","SWEPT_FACE",FACE,{"disambiguationData":[OSD([subQ0])]});Q12=makeQuery(id+"F103.opFillet","BLEND_EDGE",EDGE,{"blendedFrom":[makeQuery(id+"F99.opChamfer","BLEND_EDGE",EDGE,{"blendedFrom":[makeQuery(id+"F64.opExtrude","SWEPT_EDGE",EDGE,{"disambiguationData":[OSD([subQ0,sQuery(id+"F58.wireOp",EDGE,"E21.left")])]}),subQ1],"blendedInto":[subQ1]}),makeQuery(id+"F99.opChamfer","BLEND_EDGE",EDGE,{"blendedFrom":[makeQuery(id+"F64.opExtrude","SWEPT_EDGE",EDGE,{"disambiguationData":[OSD([subQ0,sQuery(id+"F58.wireOp",EDGE,"E21.right")])]}),subQ1],"blendedInto":[subQ1]})],"blendedInto":[]});}
            var Q13;
            {var subQ0=sQuery(id+"F54.wireOp",EDGE,"E17.right");var subQ1=makeQuery(id+"F64.opExtrude","SWEPT_FACE",FACE,{"disambiguationData":[OSD([subQ0])]});Q13=makeQuery(id+"F103.opFillet","BLEND_EDGE",EDGE,{"blendedFrom":[makeQuery(id+"F99.opChamfer","BLEND_EDGE",EDGE,{"blendedFrom":[makeQuery(id+"F64.opExtrude","SWEPT_EDGE",EDGE,{"disambiguationData":[OSD([sQuery(id+"F54.wireOp",EDGE,"E17.bottom"),subQ0])]}),subQ1],"blendedInto":[subQ1]}),makeQuery(id+"F99.opChamfer","BLEND_EDGE",EDGE,{"blendedFrom":[makeQuery(id+"F64.opExtrude","SWEPT_EDGE",EDGE,{"disambiguationData":[OSD([sQuery(id+"F54.wireOp",EDGE,"E17.top"),subQ0])]}),subQ1],"blendedInto":[subQ1]})],"blendedInto":[]});}
            var Q14;
            {var subQ0=sQuery(id+"F56.wireOp",EDGE,"E19.top");var subQ1=makeQuery(id+"F64.opExtrude","SWEPT_FACE",FACE,{"disambiguationData":[OSD([subQ0])]});Q14=makeQuery(id+"F103.opFillet","BLEND_EDGE",EDGE,{"blendedFrom":[makeQuery(id+"F99.opChamfer","BLEND_EDGE",EDGE,{"blendedFrom":[makeQuery(id+"F64.opExtrude","SWEPT_EDGE",EDGE,{"disambiguationData":[OSD([subQ0,sQuery(id+"F56.wireOp",EDGE,"E19.left")])]}),subQ1],"blendedInto":[subQ1]}),makeQuery(id+"F99.opChamfer","BLEND_EDGE",EDGE,{"blendedFrom":[makeQuery(id+"F64.opExtrude","SWEPT_EDGE",EDGE,{"disambiguationData":[OSD([subQ0,sQuery(id+"F56.wireOp",EDGE,"E19.right")])]}),subQ1],"blendedInto":[subQ1]})],"blendedInto":[]});}
            var Q15;
            {var subQ0=sQuery(id+"F66.wireOp",EDGE,"E25.top");var subQ1=makeQuery(id+"F70.opExtrude","SWEPT_FACE",FACE,{"disambiguationData":[OSD([subQ0])]});Q15=makeQuery(id+"F103.opFillet","BLEND_EDGE",EDGE,{"blendedFrom":[makeQuery(id+"F99.opChamfer","BLEND_EDGE",EDGE,{"blendedFrom":[makeQuery(id+"F70.opExtrude","SWEPT_EDGE",EDGE,{"disambiguationData":[OSD([subQ0,sQuery(id+"F66.wireOp",EDGE,"E25.left")])]}),subQ1],"blendedInto":[subQ1]}),makeQuery(id+"F99.opChamfer","BLEND_EDGE",EDGE,{"blendedFrom":[makeQuery(id+"F70.opExtrude","SWEPT_EDGE",EDGE,{"disambiguationData":[OSD([subQ0,sQuery(id+"F66.wireOp",EDGE,"E25.right")])]}),subQ1],"blendedInto":[subQ1]})],"blendedInto":[]});}
            var Q16;
            {var subQ0=sQuery(id+"F69.wireOp",EDGE,"E28.left");var subQ1=makeQuery(id+"F70.opExtrude","SWEPT_FACE",FACE,{"disambiguationData":[OSD([subQ0])]});Q16=makeQuery(id+"F103.opFillet","BLEND_EDGE",EDGE,{"blendedFrom":[makeQuery(id+"F99.opChamfer","BLEND_EDGE",EDGE,{"blendedFrom":[makeQuery(id+"F70.opExtrude","SWEPT_EDGE",EDGE,{"disambiguationData":[OSD([sQuery(id+"F69.wireOp",EDGE,"E28.bottom"),subQ0])]}),subQ1],"blendedInto":[subQ1]}),makeQuery(id+"F99.opChamfer","BLEND_EDGE",EDGE,{"blendedFrom":[makeQuery(id+"F70.opExtrude","SWEPT_EDGE",EDGE,{"disambiguationData":[OSD([sQuery(id+"F69.wireOp",EDGE,"E28.top"),subQ0])]}),subQ1],"blendedInto":[subQ1]})],"blendedInto":[]});}
            var Q17;
            {var subQ0=sQuery(id+"F68.wireOp",EDGE,"E27.bottom");var subQ1=makeQuery(id+"F70.opExtrude","SWEPT_FACE",FACE,{"disambiguationData":[OSD([subQ0])]});Q17=makeQuery(id+"F103.opFillet","BLEND_EDGE",EDGE,{"blendedFrom":[makeQuery(id+"F99.opChamfer","BLEND_EDGE",EDGE,{"blendedFrom":[makeQuery(id+"F70.opExtrude","SWEPT_EDGE",EDGE,{"disambiguationData":[OSD([subQ0,sQuery(id+"F68.wireOp",EDGE,"E27.left")])]}),subQ1],"blendedInto":[subQ1]}),makeQuery(id+"F99.opChamfer","BLEND_EDGE",EDGE,{"blendedFrom":[makeQuery(id+"F70.opExtrude","SWEPT_EDGE",EDGE,{"disambiguationData":[OSD([subQ0,sQuery(id+"F68.wireOp",EDGE,"E27.right")])]}),subQ1],"blendedInto":[subQ1]})],"blendedInto":[]});}
            var Q18;
            {var subQ0=sQuery(id+"F65.wireOp",EDGE,"E24.right");var subQ1=makeQuery(id+"F70.opExtrude","SWEPT_FACE",FACE,{"disambiguationData":[OSD([subQ0])]});Q18=makeQuery(id+"F103.opFillet","BLEND_EDGE",EDGE,{"blendedFrom":[makeQuery(id+"F99.opChamfer","BLEND_EDGE",EDGE,{"blendedFrom":[makeQuery(id+"F70.opExtrude","SWEPT_EDGE",EDGE,{"disambiguationData":[OSD([sQuery(id+"F65.wireOp",EDGE,"E24.bottom"),subQ0])]}),subQ1],"blendedInto":[subQ1]}),makeQuery(id+"F99.opChamfer","BLEND_EDGE",EDGE,{"blendedFrom":[makeQuery(id+"F70.opExtrude","SWEPT_EDGE",EDGE,{"disambiguationData":[OSD([sQuery(id+"F65.wireOp",EDGE,"E24.top"),subQ0])]}),subQ1],"blendedInto":[subQ1]})],"blendedInto":[]});}
            fillet(context, id + "F104", {"entities" : qUnion([Q0, Q1, Q2, Q3, Q4, Q5, Q6, Q7, Q8, Q9, Q10, Q11, Q12, Q13, Q14, Q15, Q16, Q17, Q18]), "radius" : 25.4 * mm, "tangentPropagation" : true, "allowEdgeOverflow" : false});
        }
    });
